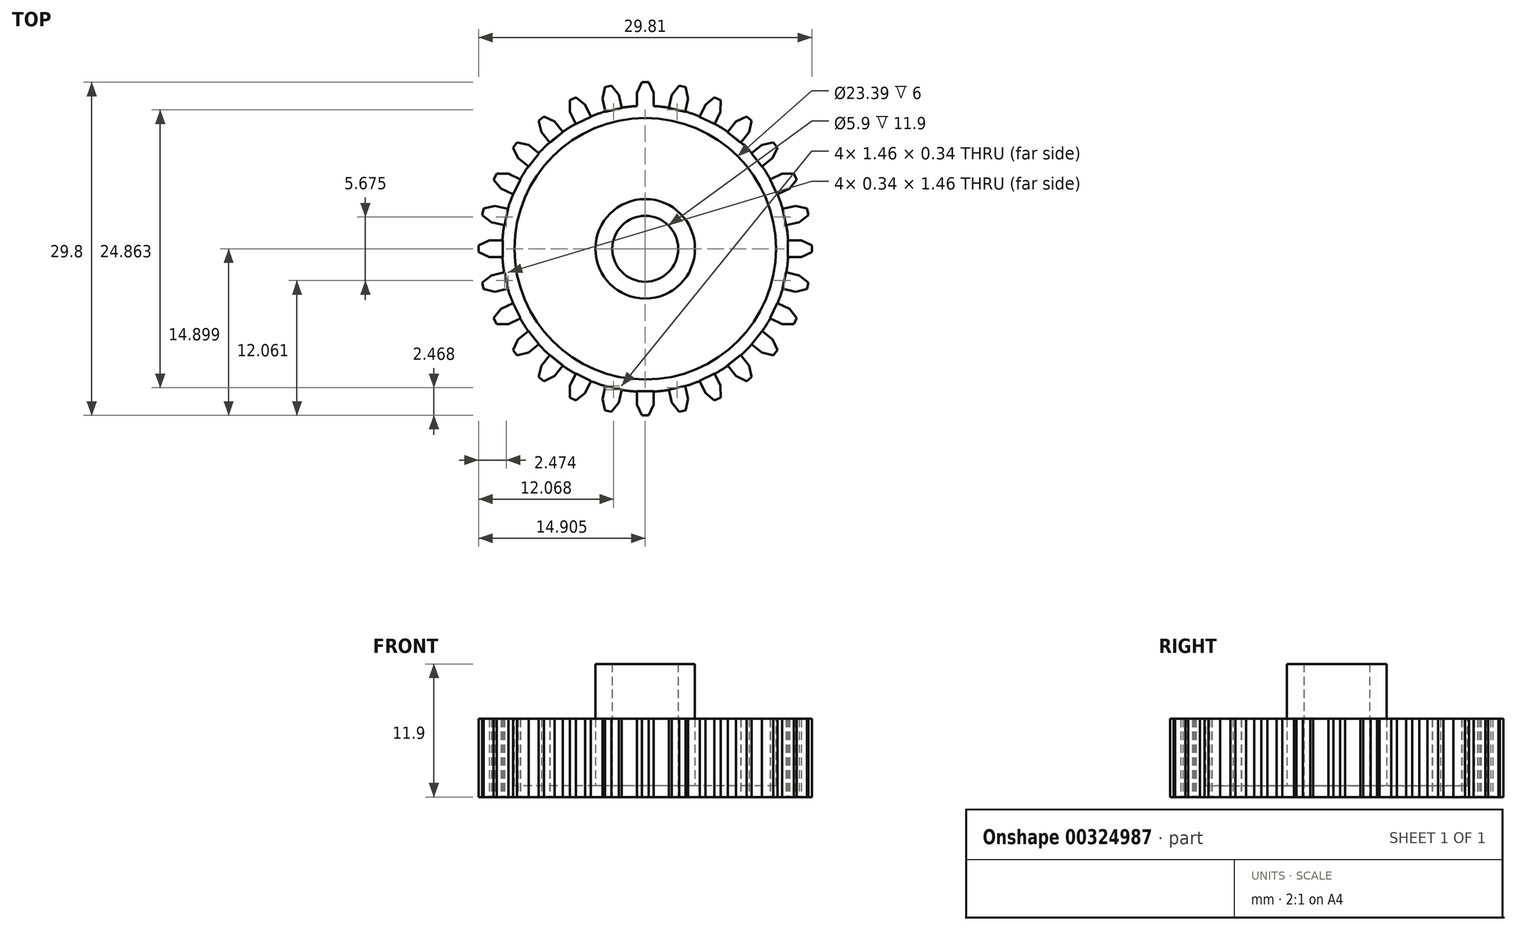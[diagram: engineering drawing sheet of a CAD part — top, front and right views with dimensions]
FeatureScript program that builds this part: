
annotation { "Feature Type Name" : "Feature", "Feature Type Description" : "" }
export const myFeature = defineFeature(function(context is Context, id is Id, definition is map)
    precondition{}
    {
        {
            var Q0;
            Q0=qCreatedBy(makeId("Top.planeOp"),FACE);
            var sketch = newSketch(context, id + "F0", { "sketchPlane" : qUnion([Q0])});
            skLineSegment(sketch, "E0", {"start": v(-37.42, 30.36) * mm, "end": v(-35.92, 30.36) * mm});
            skLineSegment(sketch, "E1", {"start": v(-36.97, 32.5) * mm, "end": v(-36.37, 32.5) * mm});
            skLineSegment(sketch, "E2", {"start": v(-37.42, 30.36) * mm, "end": v(-37.42, 31.56) * mm});
            skLineSegment(sketch, "E3", {"start": v(-37.42, 31.56) * mm, "end": v(-35.92, 31.56) * mm});
            skLineSegment(sketch, "E4", {"start": v(-35.92, 31.56) * mm, "end": v(-35.92, 30.36) * mm});
            skLineSegment(sketch, "E5", {"start": v(-36.97, 32.5) * mm, "end": v(-37.42, 31.56) * mm});
            skLineSegment(sketch, "E6", {"start": v(-36.37, 32.5) * mm, "end": v(-35.92, 31.56) * mm});
            skLineSegment(sketch, "E7.7.0", {"start": v(-36.98, 32.5) * mm, "end": v(-37.42, 31.56) * mm});
            skLineSegment(sketch, "E7.7.1", {"start": v(-35.92, 30.36) * mm, "end": v(-35.92, 31.56) * mm});
            skLineSegment(sketch, "E7.7.2", {"start": v(-36.67, 30.36) * mm, "end": v(-37.42, 30.36) * mm});
            skLineSegment(sketch, "E7.7.6", {"start": v(-36.67, 30.36) * mm, "end": v(-35.92, 30.36) * mm});
            skLineSegment(sketch, "E7.7.7", {"start": v(-36.67, 32.5) * mm, "end": v(-36.37, 32.5) * mm});
            skLineSegment(sketch, "E7.7.8", {"start": v(-36.67, 32.5) * mm, "end": v(-36.98, 32.5) * mm});
            skLineSegment(sketch, "E8", {"start": v(-36.67, 30.36) * mm, "end": v(-36.67, 4.86) * mm});
            skLineSegment(sketch, "E9", {"start": v(-36.67, 30.36) * mm, "end": v(-36.67, 17.6) * mm});
            skLineSegment(sketch, "E10.1.0", {"start": v(-40.24, 29.87) * mm, "end": v(-40.5, 31.04) * mm});
            skLineSegment(sketch, "E10.1.1", {"start": v(-38.78, 30.2) * mm, "end": v(-39.05, 31.38) * mm});
            skLineSegment(sketch, "E10.1.2", {"start": v(-40.5, 31.04) * mm, "end": v(-39.05, 31.38) * mm});
            skLineSegment(sketch, "E10.1.3", {"start": v(-40.29, 32.06) * mm, "end": v(-40.5, 31.04) * mm});
            skLineSegment(sketch, "E10.1.4", {"start": v(-39.7, 32.2) * mm, "end": v(-39.05, 31.38) * mm});
            skLineSegment(sketch, "E10.1.5", {"start": v(-40.24, 29.87) * mm, "end": v(-40.51, 31.04) * mm});
            skLineSegment(sketch, "E10.1.6", {"start": v(-39.05, 31.38) * mm, "end": v(-38.78, 30.2) * mm});
            skLineSegment(sketch, "E10.1.7", {"start": v(-40.51, 31.04) * mm, "end": v(-39.05, 31.38) * mm});
            skLineSegment(sketch, "E10.1.8", {"start": v(-40.28, 32.07) * mm, "end": v(-40.51, 31.04) * mm});
            skLineSegment(sketch, "E10.1.9", {"start": v(-39.7, 32.2) * mm, "end": v(-39.05, 31.38) * mm});
            skLineSegment(sketch, "E10.1.10", {"start": v(-39.51, 30.04) * mm, "end": v(-40.24, 29.87) * mm});
            skLineSegment(sketch, "E10.1.11", {"start": v(-40.24, 29.87) * mm, "end": v(-38.78, 30.2) * mm});
            skLineSegment(sketch, "E10.1.12", {"start": v(-39.51, 30.04) * mm, "end": v(-38.78, 30.2) * mm});
            skLineSegment(sketch, "E10.1.13", {"start": v(-40.28, 32.07) * mm, "end": v(-39.7, 32.2) * mm});
            skLineSegment(sketch, "E10.1.14", {"start": v(-39.99, 32.13) * mm, "end": v(-40.29, 32.06) * mm});
            skLineSegment(sketch, "E10.1.15", {"start": v(-39.99, 32.13) * mm, "end": v(-39.7, 32.2) * mm});
            skLineSegment(sketch, "E10.2.0", {"start": v(-42.88, 28.77) * mm, "end": v(-43.4, 29.85) * mm});
            skLineSegment(sketch, "E10.2.1", {"start": v(-41.53, 29.42) * mm, "end": v(-42.05, 30.5) * mm});
            skLineSegment(sketch, "E10.2.2", {"start": v(-43.4, 29.85) * mm, "end": v(-42.05, 30.5) * mm});
            skLineSegment(sketch, "E10.2.3", {"start": v(-43.4, 30.9) * mm, "end": v(-43.4, 29.85) * mm});
            skLineSegment(sketch, "E10.2.4", {"start": v(-42.86, 31.15) * mm, "end": v(-42.05, 30.5) * mm});
            skLineSegment(sketch, "E10.2.5", {"start": v(-42.88, 28.77) * mm, "end": v(-43.4, 29.85) * mm});
            skLineSegment(sketch, "E10.2.6", {"start": v(-42.05, 30.5) * mm, "end": v(-41.53, 29.42) * mm});
            skLineSegment(sketch, "E10.2.7", {"start": v(-43.4, 29.85) * mm, "end": v(-42.05, 30.5) * mm});
            skLineSegment(sketch, "E10.2.8", {"start": v(-43.41, 30.9) * mm, "end": v(-43.4, 29.85) * mm});
            skLineSegment(sketch, "E10.2.9", {"start": v(-42.87, 31.16) * mm, "end": v(-42.05, 30.5) * mm});
            skLineSegment(sketch, "E10.2.10", {"start": v(-42.2, 29.1) * mm, "end": v(-42.88, 28.77) * mm});
            skLineSegment(sketch, "E10.2.11", {"start": v(-42.88, 28.77) * mm, "end": v(-41.53, 29.42) * mm});
            skLineSegment(sketch, "E10.2.12", {"start": v(-42.2, 29.1) * mm, "end": v(-41.53, 29.42) * mm});
            skLineSegment(sketch, "E10.2.13", {"start": v(-43.41, 30.9) * mm, "end": v(-42.87, 31.16) * mm});
            skLineSegment(sketch, "E10.2.14", {"start": v(-43.14, 31.02) * mm, "end": v(-43.4, 30.9) * mm});
            skLineSegment(sketch, "E10.2.15", {"start": v(-43.14, 31.02) * mm, "end": v(-42.86, 31.15) * mm});
            skLineSegment(sketch, "E10.3.0", {"start": v(-45.21, 27.1) * mm, "end": v(-45.96, 28.05) * mm});
            skLineSegment(sketch, "E10.3.1", {"start": v(-44.04, 28.04) * mm, "end": v(-44.79, 28.98) * mm});
            skLineSegment(sketch, "E10.3.2", {"start": v(-45.96, 28.05) * mm, "end": v(-44.79, 28.98) * mm});
            skLineSegment(sketch, "E10.3.3", {"start": v(-46.2, 29.06) * mm, "end": v(-45.96, 28.05) * mm});
            skLineSegment(sketch, "E10.3.4", {"start": v(-45.72, 29.44) * mm, "end": v(-44.79, 28.98) * mm});
            skLineSegment(sketch, "E10.3.5", {"start": v(-45.21, 27.11) * mm, "end": v(-45.96, 28.05) * mm});
            skLineSegment(sketch, "E10.3.6", {"start": v(-44.79, 28.98) * mm, "end": v(-44.04, 28.05) * mm});
            skLineSegment(sketch, "E10.3.7", {"start": v(-45.96, 28.05) * mm, "end": v(-44.79, 28.98) * mm});
            skLineSegment(sketch, "E10.3.8", {"start": v(-46.2, 29.07) * mm, "end": v(-45.96, 28.05) * mm});
            skLineSegment(sketch, "E10.3.9", {"start": v(-45.73, 29.45) * mm, "end": v(-44.79, 28.98) * mm});
            skLineSegment(sketch, "E10.3.10", {"start": v(-44.62, 27.58) * mm, "end": v(-45.21, 27.1) * mm});
            skLineSegment(sketch, "E10.3.11", {"start": v(-45.21, 27.11) * mm, "end": v(-44.04, 28.05) * mm});
            skLineSegment(sketch, "E10.3.12", {"start": v(-44.62, 27.58) * mm, "end": v(-44.04, 28.04) * mm});
            skLineSegment(sketch, "E10.3.13", {"start": v(-46.2, 29.07) * mm, "end": v(-45.73, 29.45) * mm});
            skLineSegment(sketch, "E10.3.14", {"start": v(-45.96, 29.25) * mm, "end": v(-46.2, 29.06) * mm});
            skLineSegment(sketch, "E10.3.15", {"start": v(-45.96, 29.25) * mm, "end": v(-45.72, 29.44) * mm});
            skLineSegment(sketch, "E10.4.0", {"start": v(-47.11, 24.97) * mm, "end": v(-48.05, 25.72) * mm});
            skLineSegment(sketch, "E10.4.1", {"start": v(-46.18, 26.14) * mm, "end": v(-47.11, 26.9) * mm});
            skLineSegment(sketch, "E10.4.2", {"start": v(-48.05, 25.72) * mm, "end": v(-47.11, 26.9) * mm});
            skLineSegment(sketch, "E10.4.3", {"start": v(-48.5, 26.65) * mm, "end": v(-48.05, 25.72) * mm});
            skLineSegment(sketch, "E10.4.4", {"start": v(-48.13, 27.13) * mm, "end": v(-47.11, 26.9) * mm});
            skLineSegment(sketch, "E10.4.5", {"start": v(-47.11, 24.97) * mm, "end": v(-48.05, 25.72) * mm});
            skLineSegment(sketch, "E10.4.6", {"start": v(-47.12, 26.9) * mm, "end": v(-46.18, 26.15) * mm});
            skLineSegment(sketch, "E10.4.7", {"start": v(-48.05, 25.72) * mm, "end": v(-47.12, 26.9) * mm});
            skLineSegment(sketch, "E10.4.8", {"start": v(-48.51, 26.66) * mm, "end": v(-48.05, 25.72) * mm});
            skLineSegment(sketch, "E10.4.9", {"start": v(-48.14, 27.13) * mm, "end": v(-47.12, 26.9) * mm});
            skLineSegment(sketch, "E10.4.10", {"start": v(-46.64, 25.56) * mm, "end": v(-47.11, 24.97) * mm});
            skLineSegment(sketch, "E10.4.11", {"start": v(-47.11, 24.97) * mm, "end": v(-46.18, 26.15) * mm});
            skLineSegment(sketch, "E10.4.12", {"start": v(-46.64, 25.56) * mm, "end": v(-46.18, 26.14) * mm});
            skLineSegment(sketch, "E10.4.13", {"start": v(-48.51, 26.66) * mm, "end": v(-48.14, 27.13) * mm});
            skLineSegment(sketch, "E10.4.14", {"start": v(-48.32, 26.9) * mm, "end": v(-48.5, 26.65) * mm});
            skLineSegment(sketch, "E10.4.15", {"start": v(-48.32, 26.9) * mm, "end": v(-48.13, 27.13) * mm});
            skLineSegment(sketch, "E10.5.0", {"start": v(-48.49, 22.47) * mm, "end": v(-49.57, 22.99) * mm});
            skLineSegment(sketch, "E10.5.1", {"start": v(-47.84, 23.82) * mm, "end": v(-48.92, 24.34) * mm});
            skLineSegment(sketch, "E10.5.2", {"start": v(-49.57, 22.99) * mm, "end": v(-48.92, 24.34) * mm});
            skLineSegment(sketch, "E10.5.3", {"start": v(-50.22, 23.8) * mm, "end": v(-49.57, 22.99) * mm});
            skLineSegment(sketch, "E10.5.4", {"start": v(-49.96, 24.34) * mm, "end": v(-48.92, 24.34) * mm});
            skLineSegment(sketch, "E10.5.5", {"start": v(-48.49, 22.47) * mm, "end": v(-49.57, 22.99) * mm});
            skLineSegment(sketch, "E10.5.6", {"start": v(-48.92, 24.34) * mm, "end": v(-47.84, 23.82) * mm});
            skLineSegment(sketch, "E10.5.7", {"start": v(-49.57, 22.99) * mm, "end": v(-48.92, 24.34) * mm});
            skLineSegment(sketch, "E10.5.8", {"start": v(-50.23, 23.8) * mm, "end": v(-49.57, 22.99) * mm});
            skLineSegment(sketch, "E10.5.9", {"start": v(-49.97, 24.34) * mm, "end": v(-48.92, 24.34) * mm});
            skLineSegment(sketch, "E10.5.10", {"start": v(-48.16, 23.14) * mm, "end": v(-48.49, 22.47) * mm});
            skLineSegment(sketch, "E10.5.11", {"start": v(-48.49, 22.47) * mm, "end": v(-47.84, 23.82) * mm});
            skLineSegment(sketch, "E10.5.12", {"start": v(-48.16, 23.14) * mm, "end": v(-47.84, 23.82) * mm});
            skLineSegment(sketch, "E10.5.13", {"start": v(-50.23, 23.8) * mm, "end": v(-49.97, 24.34) * mm});
            skLineSegment(sketch, "E10.5.14", {"start": v(-50.09, 24.07) * mm, "end": v(-50.22, 23.8) * mm});
            skLineSegment(sketch, "E10.5.15", {"start": v(-50.09, 24.07) * mm, "end": v(-49.96, 24.34) * mm});
            skLineSegment(sketch, "E10.6.0", {"start": v(-49.27, 19.71) * mm, "end": v(-50.44, 19.98) * mm});
            skLineSegment(sketch, "E10.6.1", {"start": v(-48.94, 21.18) * mm, "end": v(-50.1, 21.44) * mm});
            skLineSegment(sketch, "E10.6.2", {"start": v(-50.44, 19.98) * mm, "end": v(-50.1, 21.44) * mm});
            skLineSegment(sketch, "E10.6.3", {"start": v(-51.26, 20.63) * mm, "end": v(-50.44, 19.98) * mm});
            skLineSegment(sketch, "E10.6.4", {"start": v(-51.12, 21.21) * mm, "end": v(-50.1, 21.44) * mm});
            skLineSegment(sketch, "E10.6.5", {"start": v(-49.27, 19.72) * mm, "end": v(-50.44, 19.98) * mm});
            skLineSegment(sketch, "E10.6.6", {"start": v(-50.11, 21.44) * mm, "end": v(-48.94, 21.18) * mm});
            skLineSegment(sketch, "E10.6.7", {"start": v(-50.44, 19.98) * mm, "end": v(-50.11, 21.44) * mm});
            skLineSegment(sketch, "E10.6.8", {"start": v(-51.27, 20.63) * mm, "end": v(-50.44, 19.98) * mm});
            skLineSegment(sketch, "E10.6.9", {"start": v(-51.14, 21.22) * mm, "end": v(-50.11, 21.44) * mm});
            skLineSegment(sketch, "E10.6.10", {"start": v(-49.1, 20.45) * mm, "end": v(-49.27, 19.71) * mm});
            skLineSegment(sketch, "E10.6.11", {"start": v(-49.27, 19.72) * mm, "end": v(-48.94, 21.18) * mm});
            skLineSegment(sketch, "E10.6.12", {"start": v(-49.1, 20.45) * mm, "end": v(-48.94, 21.18) * mm});
            skLineSegment(sketch, "E10.6.13", {"start": v(-51.27, 20.63) * mm, "end": v(-51.14, 21.22) * mm});
            skLineSegment(sketch, "E10.6.14", {"start": v(-51.2, 20.92) * mm, "end": v(-51.26, 20.63) * mm});
            skLineSegment(sketch, "E10.6.15", {"start": v(-51.2, 20.92) * mm, "end": v(-51.12, 21.21) * mm});
            skLineSegment(sketch, "E10.7.0", {"start": v(-49.42, 16.86) * mm, "end": v(-50.62, 16.86) * mm});
            skLineSegment(sketch, "E10.7.1", {"start": v(-49.42, 18.36) * mm, "end": v(-50.62, 18.36) * mm});
            skLineSegment(sketch, "E10.7.2", {"start": v(-50.62, 16.86) * mm, "end": v(-50.62, 18.36) * mm});
            skLineSegment(sketch, "E10.7.3", {"start": v(-51.56, 17.3) * mm, "end": v(-50.62, 16.86) * mm});
            skLineSegment(sketch, "E10.7.4", {"start": v(-51.56, 17.9) * mm, "end": v(-50.62, 18.36) * mm});
            skLineSegment(sketch, "E10.7.5", {"start": v(-49.43, 16.86) * mm, "end": v(-50.63, 16.86) * mm});
            skLineSegment(sketch, "E10.7.6", {"start": v(-50.63, 18.36) * mm, "end": v(-49.43, 18.36) * mm});
            skLineSegment(sketch, "E10.7.7", {"start": v(-50.63, 16.86) * mm, "end": v(-50.63, 18.36) * mm});
            skLineSegment(sketch, "E10.7.8", {"start": v(-51.58, 17.3) * mm, "end": v(-50.63, 16.86) * mm});
            skLineSegment(sketch, "E10.7.9", {"start": v(-51.58, 17.9) * mm, "end": v(-50.63, 18.36) * mm});
            skLineSegment(sketch, "E10.7.10", {"start": v(-49.42, 17.6) * mm, "end": v(-49.42, 16.86) * mm});
            skLineSegment(sketch, "E10.7.11", {"start": v(-49.43, 16.86) * mm, "end": v(-49.43, 18.36) * mm});
            skLineSegment(sketch, "E10.7.12", {"start": v(-49.42, 17.6) * mm, "end": v(-49.42, 18.36) * mm});
            skLineSegment(sketch, "E10.7.13", {"start": v(-51.58, 17.3) * mm, "end": v(-51.58, 17.9) * mm});
            skLineSegment(sketch, "E10.7.14", {"start": v(-51.56, 17.6) * mm, "end": v(-51.56, 17.3) * mm});
            skLineSegment(sketch, "E10.7.15", {"start": v(-51.56, 17.6) * mm, "end": v(-51.56, 17.9) * mm});
            skLineSegment(sketch, "E10.8.0", {"start": v(-48.94, 14.04) * mm, "end": v(-50.1, 13.77) * mm});
            skLineSegment(sketch, "E10.8.1", {"start": v(-49.27, 15.5) * mm, "end": v(-50.44, 15.24) * mm});
            skLineSegment(sketch, "E10.8.2", {"start": v(-50.1, 13.77) * mm, "end": v(-50.44, 15.24) * mm});
            skLineSegment(sketch, "E10.8.3", {"start": v(-51.12, 14) * mm, "end": v(-50.1, 13.77) * mm});
            skLineSegment(sketch, "E10.8.4", {"start": v(-51.26, 14.59) * mm, "end": v(-50.44, 15.24) * mm});
            skLineSegment(sketch, "E10.8.5", {"start": v(-48.94, 14.04) * mm, "end": v(-50.11, 13.77) * mm});
            skLineSegment(sketch, "E10.8.6", {"start": v(-50.44, 15.24) * mm, "end": v(-49.27, 15.5) * mm});
            skLineSegment(sketch, "E10.8.7", {"start": v(-50.11, 13.77) * mm, "end": v(-50.44, 15.24) * mm});
            skLineSegment(sketch, "E10.8.8", {"start": v(-51.14, 14) * mm, "end": v(-50.11, 13.77) * mm});
            skLineSegment(sketch, "E10.8.9", {"start": v(-51.27, 14.59) * mm, "end": v(-50.44, 15.24) * mm});
            skLineSegment(sketch, "E10.8.10", {"start": v(-49.1, 14.77) * mm, "end": v(-48.94, 14.04) * mm});
            skLineSegment(sketch, "E10.8.11", {"start": v(-48.94, 14.04) * mm, "end": v(-49.27, 15.5) * mm});
            skLineSegment(sketch, "E10.8.12", {"start": v(-49.1, 14.77) * mm, "end": v(-49.27, 15.5) * mm});
            skLineSegment(sketch, "E10.8.13", {"start": v(-51.14, 14) * mm, "end": v(-51.27, 14.59) * mm});
            skLineSegment(sketch, "E10.8.14", {"start": v(-51.2, 14.3) * mm, "end": v(-51.12, 14) * mm});
            skLineSegment(sketch, "E10.8.15", {"start": v(-51.2, 14.3) * mm, "end": v(-51.26, 14.59) * mm});
            skLineSegment(sketch, "E10.9.0", {"start": v(-47.84, 11.4) * mm, "end": v(-48.92, 10.88) * mm});
            skLineSegment(sketch, "E10.9.1", {"start": v(-48.49, 12.75) * mm, "end": v(-49.57, 12.23) * mm});
            skLineSegment(sketch, "E10.9.2", {"start": v(-48.92, 10.88) * mm, "end": v(-49.57, 12.23) * mm});
            skLineSegment(sketch, "E10.9.3", {"start": v(-49.96, 10.87) * mm, "end": v(-48.92, 10.88) * mm});
            skLineSegment(sketch, "E10.9.4", {"start": v(-50.22, 11.42) * mm, "end": v(-49.57, 12.23) * mm});
            skLineSegment(sketch, "E10.9.5", {"start": v(-47.84, 11.4) * mm, "end": v(-48.92, 10.88) * mm});
            skLineSegment(sketch, "E10.9.6", {"start": v(-49.57, 12.23) * mm, "end": v(-48.49, 12.75) * mm});
            skLineSegment(sketch, "E10.9.7", {"start": v(-48.92, 10.88) * mm, "end": v(-49.57, 12.23) * mm});
            skLineSegment(sketch, "E10.9.8", {"start": v(-49.97, 10.87) * mm, "end": v(-48.92, 10.88) * mm});
            skLineSegment(sketch, "E10.9.9", {"start": v(-50.23, 11.41) * mm, "end": v(-49.57, 12.23) * mm});
            skLineSegment(sketch, "E10.9.10", {"start": v(-48.16, 12.08) * mm, "end": v(-47.84, 11.4) * mm});
            skLineSegment(sketch, "E10.9.11", {"start": v(-47.84, 11.4) * mm, "end": v(-48.49, 12.75) * mm});
            skLineSegment(sketch, "E10.9.12", {"start": v(-48.16, 12.08) * mm, "end": v(-48.49, 12.75) * mm});
            skLineSegment(sketch, "E10.9.13", {"start": v(-49.97, 10.87) * mm, "end": v(-50.23, 11.41) * mm});
            skLineSegment(sketch, "E10.9.14", {"start": v(-50.09, 11.15) * mm, "end": v(-49.96, 10.87) * mm});
            skLineSegment(sketch, "E10.9.15", {"start": v(-50.09, 11.15) * mm, "end": v(-50.22, 11.42) * mm});
            skLineSegment(sketch, "E10.10.0", {"start": v(-46.18, 9.07) * mm, "end": v(-47.11, 8.32) * mm});
            skLineSegment(sketch, "E10.10.1", {"start": v(-47.11, 10.25) * mm, "end": v(-48.05, 9.5) * mm});
            skLineSegment(sketch, "E10.10.2", {"start": v(-47.11, 8.32) * mm, "end": v(-48.05, 9.5) * mm});
            skLineSegment(sketch, "E10.10.3", {"start": v(-48.13, 8.09) * mm, "end": v(-47.11, 8.32) * mm});
            skLineSegment(sketch, "E10.10.4", {"start": v(-48.5, 8.56) * mm, "end": v(-48.05, 9.5) * mm});
            skLineSegment(sketch, "E10.10.5", {"start": v(-46.18, 9.07) * mm, "end": v(-47.12, 8.32) * mm});
            skLineSegment(sketch, "E10.10.6", {"start": v(-48.05, 9.5) * mm, "end": v(-47.11, 10.24) * mm});
            skLineSegment(sketch, "E10.10.7", {"start": v(-47.12, 8.32) * mm, "end": v(-48.05, 9.5) * mm});
            skLineSegment(sketch, "E10.10.8", {"start": v(-48.14, 8.08) * mm, "end": v(-47.12, 8.32) * mm});
            skLineSegment(sketch, "E10.10.9", {"start": v(-48.51, 8.55) * mm, "end": v(-48.05, 9.5) * mm});
            skLineSegment(sketch, "E10.10.10", {"start": v(-46.64, 9.66) * mm, "end": v(-46.18, 9.07) * mm});
            skLineSegment(sketch, "E10.10.11", {"start": v(-46.18, 9.07) * mm, "end": v(-47.11, 10.24) * mm});
            skLineSegment(sketch, "E10.10.12", {"start": v(-46.64, 9.66) * mm, "end": v(-47.11, 10.25) * mm});
            skLineSegment(sketch, "E10.10.13", {"start": v(-48.14, 8.08) * mm, "end": v(-48.51, 8.55) * mm});
            skLineSegment(sketch, "E10.10.14", {"start": v(-48.32, 8.33) * mm, "end": v(-48.13, 8.09) * mm});
            skLineSegment(sketch, "E10.10.15", {"start": v(-48.32, 8.33) * mm, "end": v(-48.5, 8.56) * mm});
            skLineSegment(sketch, "E10.11.0", {"start": v(-44.04, 7.17) * mm, "end": v(-44.79, 6.23) * mm});
            skLineSegment(sketch, "E10.11.1", {"start": v(-45.21, 8.1) * mm, "end": v(-45.96, 7.17) * mm});
            skLineSegment(sketch, "E10.11.2", {"start": v(-44.79, 6.23) * mm, "end": v(-45.96, 7.17) * mm});
            skLineSegment(sketch, "E10.11.3", {"start": v(-45.72, 5.78) * mm, "end": v(-44.79, 6.23) * mm});
            skLineSegment(sketch, "E10.11.4", {"start": v(-46.2, 6.15) * mm, "end": v(-45.96, 7.17) * mm});
            skLineSegment(sketch, "E10.11.5", {"start": v(-44.04, 7.17) * mm, "end": v(-44.79, 6.23) * mm});
            skLineSegment(sketch, "E10.11.6", {"start": v(-45.96, 7.17) * mm, "end": v(-45.21, 8.1) * mm});
            skLineSegment(sketch, "E10.11.7", {"start": v(-44.79, 6.23) * mm, "end": v(-45.96, 7.17) * mm});
            skLineSegment(sketch, "E10.11.8", {"start": v(-45.73, 5.77) * mm, "end": v(-44.79, 6.23) * mm});
            skLineSegment(sketch, "E10.11.9", {"start": v(-46.2, 6.15) * mm, "end": v(-45.96, 7.17) * mm});
            skLineSegment(sketch, "E10.11.10", {"start": v(-44.62, 7.64) * mm, "end": v(-44.04, 7.17) * mm});
            skLineSegment(sketch, "E10.11.11", {"start": v(-44.04, 7.17) * mm, "end": v(-45.21, 8.1) * mm});
            skLineSegment(sketch, "E10.11.12", {"start": v(-44.62, 7.64) * mm, "end": v(-45.21, 8.1) * mm});
            skLineSegment(sketch, "E10.11.13", {"start": v(-45.73, 5.77) * mm, "end": v(-46.2, 6.15) * mm});
            skLineSegment(sketch, "E10.11.14", {"start": v(-45.96, 5.97) * mm, "end": v(-45.72, 5.78) * mm});
            skLineSegment(sketch, "E10.11.15", {"start": v(-45.96, 5.97) * mm, "end": v(-46.2, 6.15) * mm});
            skLineSegment(sketch, "E10.12.0", {"start": v(-41.53, 5.8) * mm, "end": v(-42.05, 4.71) * mm});
            skLineSegment(sketch, "E10.12.1", {"start": v(-42.88, 6.45) * mm, "end": v(-43.4, 5.37) * mm});
            skLineSegment(sketch, "E10.12.2", {"start": v(-42.05, 4.71) * mm, "end": v(-43.4, 5.37) * mm});
            skLineSegment(sketch, "E10.12.3", {"start": v(-42.86, 4.06) * mm, "end": v(-42.05, 4.71) * mm});
            skLineSegment(sketch, "E10.12.4", {"start": v(-43.4, 4.32) * mm, "end": v(-43.4, 5.37) * mm});
            skLineSegment(sketch, "E10.12.5", {"start": v(-41.53, 5.8) * mm, "end": v(-42.05, 4.71) * mm});
            skLineSegment(sketch, "E10.12.6", {"start": v(-43.4, 5.36) * mm, "end": v(-42.88, 6.45) * mm});
            skLineSegment(sketch, "E10.12.7", {"start": v(-42.05, 4.71) * mm, "end": v(-43.4, 5.36) * mm});
            skLineSegment(sketch, "E10.12.8", {"start": v(-42.87, 4.05) * mm, "end": v(-42.05, 4.71) * mm});
            skLineSegment(sketch, "E10.12.9", {"start": v(-43.41, 4.31) * mm, "end": v(-43.4, 5.36) * mm});
            skLineSegment(sketch, "E10.12.10", {"start": v(-42.2, 6.12) * mm, "end": v(-41.53, 5.8) * mm});
            skLineSegment(sketch, "E10.12.11", {"start": v(-41.53, 5.8) * mm, "end": v(-42.88, 6.45) * mm});
            skLineSegment(sketch, "E10.12.12", {"start": v(-42.2, 6.12) * mm, "end": v(-42.88, 6.45) * mm});
            skLineSegment(sketch, "E10.12.13", {"start": v(-42.87, 4.05) * mm, "end": v(-43.41, 4.31) * mm});
            skLineSegment(sketch, "E10.12.14", {"start": v(-43.14, 4.2) * mm, "end": v(-42.86, 4.06) * mm});
            skLineSegment(sketch, "E10.12.15", {"start": v(-43.14, 4.2) * mm, "end": v(-43.4, 4.32) * mm});
            skLineSegment(sketch, "E10.13.0", {"start": v(-38.78, 5.01) * mm, "end": v(-39.05, 3.84) * mm});
            skLineSegment(sketch, "E10.13.1", {"start": v(-40.24, 5.35) * mm, "end": v(-40.5, 4.18) * mm});
            skLineSegment(sketch, "E10.13.2", {"start": v(-39.05, 3.84) * mm, "end": v(-40.5, 4.18) * mm});
            skLineSegment(sketch, "E10.13.3", {"start": v(-39.7, 3.02) * mm, "end": v(-39.05, 3.84) * mm});
            skLineSegment(sketch, "E10.13.4", {"start": v(-40.28, 3.16) * mm, "end": v(-40.5, 4.18) * mm});
            skLineSegment(sketch, "E10.13.5", {"start": v(-38.78, 5) * mm, "end": v(-39.05, 3.84) * mm});
            skLineSegment(sketch, "E10.13.6", {"start": v(-40.51, 4.17) * mm, "end": v(-40.24, 5.34) * mm});
            skLineSegment(sketch, "E10.13.7", {"start": v(-39.05, 3.84) * mm, "end": v(-40.51, 4.17) * mm});
            skLineSegment(sketch, "E10.13.8", {"start": v(-39.7, 3.01) * mm, "end": v(-39.05, 3.84) * mm});
            skLineSegment(sketch, "E10.13.9", {"start": v(-40.28, 3.15) * mm, "end": v(-40.51, 4.17) * mm});
            skLineSegment(sketch, "E10.13.10", {"start": v(-39.51, 5.18) * mm, "end": v(-38.78, 5.01) * mm});
            skLineSegment(sketch, "E10.13.11", {"start": v(-38.78, 5) * mm, "end": v(-40.24, 5.34) * mm});
            skLineSegment(sketch, "E10.13.12", {"start": v(-39.51, 5.18) * mm, "end": v(-40.24, 5.35) * mm});
            skLineSegment(sketch, "E10.13.13", {"start": v(-39.7, 3.01) * mm, "end": v(-40.28, 3.15) * mm});
            skLineSegment(sketch, "E10.13.14", {"start": v(-39.99, 3.1) * mm, "end": v(-39.7, 3.02) * mm});
            skLineSegment(sketch, "E10.13.15", {"start": v(-39.99, 3.1) * mm, "end": v(-40.28, 3.16) * mm});
            skLineSegment(sketch, "E10.14.0", {"start": v(-35.92, 4.86) * mm, "end": v(-35.92, 3.66) * mm});
            skLineSegment(sketch, "E10.14.1", {"start": v(-37.42, 4.86) * mm, "end": v(-37.42, 3.66) * mm});
            skLineSegment(sketch, "E10.14.2", {"start": v(-35.92, 3.66) * mm, "end": v(-37.42, 3.66) * mm});
            skLineSegment(sketch, "E10.14.3", {"start": v(-36.37, 2.72) * mm, "end": v(-35.92, 3.66) * mm});
            skLineSegment(sketch, "E10.14.4", {"start": v(-36.97, 2.72) * mm, "end": v(-37.42, 3.66) * mm});
            skLineSegment(sketch, "E10.14.5", {"start": v(-35.92, 4.86) * mm, "end": v(-35.92, 3.66) * mm});
            skLineSegment(sketch, "E10.14.6", {"start": v(-37.42, 3.66) * mm, "end": v(-37.42, 4.86) * mm});
            skLineSegment(sketch, "E10.14.7", {"start": v(-35.92, 3.66) * mm, "end": v(-37.42, 3.66) * mm});
            skLineSegment(sketch, "E10.14.8", {"start": v(-36.37, 2.7) * mm, "end": v(-35.92, 3.66) * mm});
            skLineSegment(sketch, "E10.14.9", {"start": v(-36.97, 2.7) * mm, "end": v(-37.42, 3.66) * mm});
            skLineSegment(sketch, "E10.14.10", {"start": v(-36.67, 4.86) * mm, "end": v(-35.92, 4.86) * mm});
            skLineSegment(sketch, "E10.14.11", {"start": v(-35.92, 4.86) * mm, "end": v(-37.42, 4.86) * mm});
            skLineSegment(sketch, "E10.14.12", {"start": v(-36.67, 4.86) * mm, "end": v(-37.42, 4.86) * mm});
            skLineSegment(sketch, "E10.14.13", {"start": v(-36.37, 2.7) * mm, "end": v(-36.97, 2.7) * mm});
            skLineSegment(sketch, "E10.14.14", {"start": v(-36.67, 2.72) * mm, "end": v(-36.37, 2.72) * mm});
            skLineSegment(sketch, "E10.14.15", {"start": v(-36.67, 2.72) * mm, "end": v(-36.97, 2.72) * mm});
            skLineSegment(sketch, "E10.15.0", {"start": v(-33.1, 5.35) * mm, "end": v(-32.84, 4.18) * mm});
            skLineSegment(sketch, "E10.15.1", {"start": v(-34.57, 5.01) * mm, "end": v(-34.3, 3.84) * mm});
            skLineSegment(sketch, "E10.15.2", {"start": v(-32.84, 4.18) * mm, "end": v(-34.3, 3.84) * mm});
            skLineSegment(sketch, "E10.15.3", {"start": v(-33.06, 3.16) * mm, "end": v(-32.84, 4.18) * mm});
            skLineSegment(sketch, "E10.15.4", {"start": v(-33.65, 3.03) * mm, "end": v(-34.3, 3.84) * mm});
            skLineSegment(sketch, "E10.15.5", {"start": v(-33.1, 5.34) * mm, "end": v(-32.84, 4.17) * mm});
            skLineSegment(sketch, "E10.15.6", {"start": v(-34.3, 3.84) * mm, "end": v(-34.57, 5) * mm});
            skLineSegment(sketch, "E10.15.7", {"start": v(-32.84, 4.17) * mm, "end": v(-34.3, 3.84) * mm});
            skLineSegment(sketch, "E10.15.8", {"start": v(-33.07, 3.15) * mm, "end": v(-32.84, 4.17) * mm});
            skLineSegment(sketch, "E10.15.9", {"start": v(-33.65, 3.01) * mm, "end": v(-34.3, 3.84) * mm});
            skLineSegment(sketch, "E10.15.10", {"start": v(-33.84, 5.18) * mm, "end": v(-33.1, 5.35) * mm});
            skLineSegment(sketch, "E10.15.11", {"start": v(-33.1, 5.34) * mm, "end": v(-34.57, 5) * mm});
            skLineSegment(sketch, "E10.15.12", {"start": v(-33.84, 5.18) * mm, "end": v(-34.57, 5.01) * mm});
            skLineSegment(sketch, "E10.15.13", {"start": v(-33.07, 3.15) * mm, "end": v(-33.65, 3.01) * mm});
            skLineSegment(sketch, "E10.15.14", {"start": v(-33.36, 3.1) * mm, "end": v(-33.06, 3.16) * mm});
            skLineSegment(sketch, "E10.15.15", {"start": v(-33.36, 3.1) * mm, "end": v(-33.65, 3.03) * mm});
            skLineSegment(sketch, "E10.16.0", {"start": v(-30.47, 6.45) * mm, "end": v(-29.95, 5.37) * mm});
            skLineSegment(sketch, "E10.16.1", {"start": v(-31.82, 5.8) * mm, "end": v(-31.3, 4.71) * mm});
            skLineSegment(sketch, "E10.16.2", {"start": v(-29.95, 5.37) * mm, "end": v(-31.3, 4.71) * mm});
            skLineSegment(sketch, "E10.16.3", {"start": v(-29.94, 4.33) * mm, "end": v(-29.95, 5.37) * mm});
            skLineSegment(sketch, "E10.16.4", {"start": v(-30.48, 4.06) * mm, "end": v(-31.3, 4.71) * mm});
            skLineSegment(sketch, "E10.16.5", {"start": v(-30.47, 6.45) * mm, "end": v(-29.95, 5.36) * mm});
            skLineSegment(sketch, "E10.16.6", {"start": v(-31.3, 4.71) * mm, "end": v(-31.82, 5.8) * mm});
            skLineSegment(sketch, "E10.16.7", {"start": v(-29.95, 5.36) * mm, "end": v(-31.3, 4.71) * mm});
            skLineSegment(sketch, "E10.16.8", {"start": v(-29.94, 4.31) * mm, "end": v(-29.95, 5.36) * mm});
            skLineSegment(sketch, "E10.16.9", {"start": v(-30.48, 4.05) * mm, "end": v(-31.3, 4.71) * mm});
            skLineSegment(sketch, "E10.16.10", {"start": v(-31.14, 6.12) * mm, "end": v(-30.47, 6.45) * mm});
            skLineSegment(sketch, "E10.16.11", {"start": v(-30.47, 6.45) * mm, "end": v(-31.82, 5.8) * mm});
            skLineSegment(sketch, "E10.16.12", {"start": v(-31.14, 6.12) * mm, "end": v(-31.82, 5.8) * mm});
            skLineSegment(sketch, "E10.16.13", {"start": v(-29.94, 4.31) * mm, "end": v(-30.48, 4.05) * mm});
            skLineSegment(sketch, "E10.16.14", {"start": v(-30.21, 4.2) * mm, "end": v(-29.94, 4.33) * mm});
            skLineSegment(sketch, "E10.16.15", {"start": v(-30.21, 4.2) * mm, "end": v(-30.48, 4.06) * mm});
            skLineSegment(sketch, "E10.17.0", {"start": v(-28.14, 8.1) * mm, "end": v(-27.4, 7.17) * mm});
            skLineSegment(sketch, "E10.17.1", {"start": v(-29.31, 7.17) * mm, "end": v(-28.56, 6.23) * mm});
            skLineSegment(sketch, "E10.17.2", {"start": v(-27.4, 7.17) * mm, "end": v(-28.56, 6.23) * mm});
            skLineSegment(sketch, "E10.17.3", {"start": v(-27.15, 6.16) * mm, "end": v(-27.4, 7.17) * mm});
            skLineSegment(sketch, "E10.17.4", {"start": v(-27.63, 5.78) * mm, "end": v(-28.56, 6.23) * mm});
            skLineSegment(sketch, "E10.17.5", {"start": v(-28.14, 8.1) * mm, "end": v(-27.39, 7.17) * mm});
            skLineSegment(sketch, "E10.17.6", {"start": v(-28.56, 6.23) * mm, "end": v(-29.31, 7.17) * mm});
            skLineSegment(sketch, "E10.17.7", {"start": v(-27.39, 7.17) * mm, "end": v(-28.56, 6.23) * mm});
            skLineSegment(sketch, "E10.17.8", {"start": v(-27.15, 6.15) * mm, "end": v(-27.39, 7.17) * mm});
            skLineSegment(sketch, "E10.17.9", {"start": v(-27.62, 5.77) * mm, "end": v(-28.56, 6.23) * mm});
            skLineSegment(sketch, "E10.17.10", {"start": v(-28.73, 7.64) * mm, "end": v(-28.14, 8.1) * mm});
            skLineSegment(sketch, "E10.17.11", {"start": v(-28.14, 8.1) * mm, "end": v(-29.31, 7.17) * mm});
            skLineSegment(sketch, "E10.17.12", {"start": v(-28.73, 7.64) * mm, "end": v(-29.31, 7.17) * mm});
            skLineSegment(sketch, "E10.17.13", {"start": v(-27.15, 6.15) * mm, "end": v(-27.62, 5.77) * mm});
            skLineSegment(sketch, "E10.17.14", {"start": v(-27.4, 5.97) * mm, "end": v(-27.15, 6.16) * mm});
            skLineSegment(sketch, "E10.17.15", {"start": v(-27.4, 5.97) * mm, "end": v(-27.63, 5.78) * mm});
            skLineSegment(sketch, "E10.18.0", {"start": v(-26.24, 10.25) * mm, "end": v(-25.3, 9.5) * mm});
            skLineSegment(sketch, "E10.18.1", {"start": v(-27.17, 9.07) * mm, "end": v(-26.24, 8.32) * mm});
            skLineSegment(sketch, "E10.18.2", {"start": v(-25.3, 9.5) * mm, "end": v(-26.24, 8.32) * mm});
            skLineSegment(sketch, "E10.18.3", {"start": v(-24.84, 8.56) * mm, "end": v(-25.3, 9.5) * mm});
            skLineSegment(sketch, "E10.18.4", {"start": v(-25.22, 8.1) * mm, "end": v(-26.24, 8.32) * mm});
            skLineSegment(sketch, "E10.18.5", {"start": v(-26.24, 10.24) * mm, "end": v(-25.3, 9.5) * mm});
            skLineSegment(sketch, "E10.18.6", {"start": v(-26.23, 8.32) * mm, "end": v(-27.17, 9.07) * mm});
            skLineSegment(sketch, "E10.18.7", {"start": v(-25.3, 9.5) * mm, "end": v(-26.23, 8.32) * mm});
            skLineSegment(sketch, "E10.18.8", {"start": v(-24.84, 8.55) * mm, "end": v(-25.3, 9.5) * mm});
            skLineSegment(sketch, "E10.18.9", {"start": v(-25.21, 8.08) * mm, "end": v(-26.23, 8.32) * mm});
            skLineSegment(sketch, "E10.18.10", {"start": v(-26.7, 9.66) * mm, "end": v(-26.24, 10.25) * mm});
            skLineSegment(sketch, "E10.18.11", {"start": v(-26.24, 10.24) * mm, "end": v(-27.17, 9.07) * mm});
            skLineSegment(sketch, "E10.18.12", {"start": v(-26.7, 9.66) * mm, "end": v(-27.17, 9.07) * mm});
            skLineSegment(sketch, "E10.18.13", {"start": v(-24.84, 8.55) * mm, "end": v(-25.21, 8.08) * mm});
            skLineSegment(sketch, "E10.18.14", {"start": v(-25.03, 8.33) * mm, "end": v(-24.84, 8.56) * mm});
            skLineSegment(sketch, "E10.18.15", {"start": v(-25.03, 8.33) * mm, "end": v(-25.22, 8.1) * mm});
            skLineSegment(sketch, "E10.19.0", {"start": v(-24.86, 12.75) * mm, "end": v(-23.78, 12.23) * mm});
            skLineSegment(sketch, "E10.19.1", {"start": v(-25.51, 11.4) * mm, "end": v(-24.43, 10.88) * mm});
            skLineSegment(sketch, "E10.19.2", {"start": v(-23.78, 12.23) * mm, "end": v(-24.43, 10.88) * mm});
            skLineSegment(sketch, "E10.19.3", {"start": v(-23.13, 11.42) * mm, "end": v(-23.78, 12.23) * mm});
            skLineSegment(sketch, "E10.19.4", {"start": v(-23.39, 10.88) * mm, "end": v(-24.43, 10.88) * mm});
            skLineSegment(sketch, "E10.19.5", {"start": v(-24.86, 12.75) * mm, "end": v(-23.78, 12.23) * mm});
            skLineSegment(sketch, "E10.19.6", {"start": v(-24.43, 10.88) * mm, "end": v(-25.51, 11.4) * mm});
            skLineSegment(sketch, "E10.19.7", {"start": v(-23.78, 12.23) * mm, "end": v(-24.43, 10.88) * mm});
            skLineSegment(sketch, "E10.19.8", {"start": v(-23.12, 11.41) * mm, "end": v(-23.78, 12.23) * mm});
            skLineSegment(sketch, "E10.19.9", {"start": v(-23.38, 10.87) * mm, "end": v(-24.43, 10.88) * mm});
            skLineSegment(sketch, "E10.19.10", {"start": v(-25.19, 12.08) * mm, "end": v(-24.86, 12.75) * mm});
            skLineSegment(sketch, "E10.19.11", {"start": v(-24.86, 12.75) * mm, "end": v(-25.51, 11.4) * mm});
            skLineSegment(sketch, "E10.19.12", {"start": v(-25.19, 12.08) * mm, "end": v(-25.51, 11.4) * mm});
            skLineSegment(sketch, "E10.19.13", {"start": v(-23.12, 11.41) * mm, "end": v(-23.38, 10.87) * mm});
            skLineSegment(sketch, "E10.19.14", {"start": v(-23.26, 11.15) * mm, "end": v(-23.13, 11.42) * mm});
            skLineSegment(sketch, "E10.19.15", {"start": v(-23.26, 11.15) * mm, "end": v(-23.39, 10.88) * mm});
            skLineSegment(sketch, "E10.20.0", {"start": v(-24.08, 15.5) * mm, "end": v(-22.9, 15.24) * mm});
            skLineSegment(sketch, "E10.20.1", {"start": v(-24.41, 14.04) * mm, "end": v(-23.24, 13.77) * mm});
            skLineSegment(sketch, "E10.20.2", {"start": v(-22.9, 15.24) * mm, "end": v(-23.24, 13.77) * mm});
            skLineSegment(sketch, "E10.20.3", {"start": v(-22.1, 14.6) * mm, "end": v(-22.9, 15.24) * mm});
            skLineSegment(sketch, "E10.20.4", {"start": v(-22.22, 14) * mm, "end": v(-23.24, 13.77) * mm});
            skLineSegment(sketch, "E10.20.5", {"start": v(-24.08, 15.5) * mm, "end": v(-22.9, 15.24) * mm});
            skLineSegment(sketch, "E10.20.6", {"start": v(-23.24, 13.77) * mm, "end": v(-24.4, 14.04) * mm});
            skLineSegment(sketch, "E10.20.7", {"start": v(-22.9, 15.24) * mm, "end": v(-23.24, 13.77) * mm});
            skLineSegment(sketch, "E10.20.8", {"start": v(-22.08, 14.59) * mm, "end": v(-22.9, 15.24) * mm});
            skLineSegment(sketch, "E10.20.9", {"start": v(-22.21, 14) * mm, "end": v(-23.24, 13.77) * mm});
            skLineSegment(sketch, "E10.20.10", {"start": v(-24.24, 14.77) * mm, "end": v(-24.08, 15.5) * mm});
            skLineSegment(sketch, "E10.20.11", {"start": v(-24.08, 15.5) * mm, "end": v(-24.4, 14.04) * mm});
            skLineSegment(sketch, "E10.20.12", {"start": v(-24.24, 14.77) * mm, "end": v(-24.41, 14.04) * mm});
            skLineSegment(sketch, "E10.20.13", {"start": v(-22.08, 14.59) * mm, "end": v(-22.21, 14) * mm});
            skLineSegment(sketch, "E10.20.14", {"start": v(-22.16, 14.3) * mm, "end": v(-22.1, 14.6) * mm});
            skLineSegment(sketch, "E10.20.15", {"start": v(-22.16, 14.3) * mm, "end": v(-22.22, 14) * mm});
            skLineSegment(sketch, "E10.21.0", {"start": v(-23.92, 18.36) * mm, "end": v(-22.72, 18.36) * mm});
            skLineSegment(sketch, "E10.21.1", {"start": v(-23.92, 16.86) * mm, "end": v(-22.72, 16.86) * mm});
            skLineSegment(sketch, "E10.21.2", {"start": v(-22.72, 18.36) * mm, "end": v(-22.72, 16.86) * mm});
            skLineSegment(sketch, "E10.21.3", {"start": v(-21.78, 17.91) * mm, "end": v(-22.72, 18.36) * mm});
            skLineSegment(sketch, "E10.21.4", {"start": v(-21.78, 17.3) * mm, "end": v(-22.72, 16.86) * mm});
            skLineSegment(sketch, "E10.21.5", {"start": v(-23.92, 18.36) * mm, "end": v(-22.72, 18.36) * mm});
            skLineSegment(sketch, "E10.21.6", {"start": v(-22.72, 16.86) * mm, "end": v(-23.92, 16.86) * mm});
            skLineSegment(sketch, "E10.21.7", {"start": v(-22.72, 18.36) * mm, "end": v(-22.72, 16.86) * mm});
            skLineSegment(sketch, "E10.21.8", {"start": v(-21.77, 17.9) * mm, "end": v(-22.72, 18.36) * mm});
            skLineSegment(sketch, "E10.21.9", {"start": v(-21.77, 17.3) * mm, "end": v(-22.72, 16.86) * mm});
            skLineSegment(sketch, "E10.21.10", {"start": v(-23.92, 17.6) * mm, "end": v(-23.92, 18.36) * mm});
            skLineSegment(sketch, "E10.21.11", {"start": v(-23.92, 18.36) * mm, "end": v(-23.92, 16.86) * mm});
            skLineSegment(sketch, "E10.21.12", {"start": v(-23.92, 17.6) * mm, "end": v(-23.92, 16.86) * mm});
            skLineSegment(sketch, "E10.21.13", {"start": v(-21.77, 17.9) * mm, "end": v(-21.77, 17.3) * mm});
            skLineSegment(sketch, "E10.21.14", {"start": v(-21.78, 17.6) * mm, "end": v(-21.78, 17.91) * mm});
            skLineSegment(sketch, "E10.21.15", {"start": v(-21.78, 17.6) * mm, "end": v(-21.78, 17.3) * mm});
            skLineSegment(sketch, "E10.22.0", {"start": v(-24.41, 21.18) * mm, "end": v(-23.24, 21.44) * mm});
            skLineSegment(sketch, "E10.22.1", {"start": v(-24.08, 19.71) * mm, "end": v(-22.9, 19.98) * mm});
            skLineSegment(sketch, "E10.22.2", {"start": v(-23.24, 21.44) * mm, "end": v(-22.9, 19.98) * mm});
            skLineSegment(sketch, "E10.22.3", {"start": v(-22.23, 21.22) * mm, "end": v(-23.24, 21.44) * mm});
            skLineSegment(sketch, "E10.22.4", {"start": v(-22.1, 20.63) * mm, "end": v(-22.9, 19.98) * mm});
            skLineSegment(sketch, "E10.22.5", {"start": v(-24.4, 21.18) * mm, "end": v(-23.24, 21.44) * mm});
            skLineSegment(sketch, "E10.22.6", {"start": v(-22.9, 19.98) * mm, "end": v(-24.08, 19.72) * mm});
            skLineSegment(sketch, "E10.22.7", {"start": v(-23.24, 21.44) * mm, "end": v(-22.9, 19.98) * mm});
            skLineSegment(sketch, "E10.22.8", {"start": v(-22.21, 21.22) * mm, "end": v(-23.24, 21.44) * mm});
            skLineSegment(sketch, "E10.22.9", {"start": v(-22.08, 20.63) * mm, "end": v(-22.9, 19.98) * mm});
            skLineSegment(sketch, "E10.22.10", {"start": v(-24.24, 20.45) * mm, "end": v(-24.41, 21.18) * mm});
            skLineSegment(sketch, "E10.22.11", {"start": v(-24.4, 21.18) * mm, "end": v(-24.08, 19.72) * mm});
            skLineSegment(sketch, "E10.22.12", {"start": v(-24.24, 20.45) * mm, "end": v(-24.08, 19.71) * mm});
            skLineSegment(sketch, "E10.22.13", {"start": v(-22.21, 21.22) * mm, "end": v(-22.08, 20.63) * mm});
            skLineSegment(sketch, "E10.22.14", {"start": v(-22.16, 20.92) * mm, "end": v(-22.23, 21.22) * mm});
            skLineSegment(sketch, "E10.22.15", {"start": v(-22.16, 20.92) * mm, "end": v(-22.1, 20.63) * mm});
            skLineSegment(sketch, "E10.23.0", {"start": v(-25.51, 23.82) * mm, "end": v(-24.43, 24.34) * mm});
            skLineSegment(sketch, "E10.23.1", {"start": v(-24.86, 22.47) * mm, "end": v(-23.78, 22.99) * mm});
            skLineSegment(sketch, "E10.23.2", {"start": v(-24.43, 24.34) * mm, "end": v(-23.78, 22.99) * mm});
            skLineSegment(sketch, "E10.23.3", {"start": v(-23.4, 24.34) * mm, "end": v(-24.43, 24.34) * mm});
            skLineSegment(sketch, "E10.23.4", {"start": v(-23.13, 23.8) * mm, "end": v(-23.78, 22.99) * mm});
            skLineSegment(sketch, "E10.23.5", {"start": v(-25.51, 23.82) * mm, "end": v(-24.43, 24.34) * mm});
            skLineSegment(sketch, "E10.23.6", {"start": v(-23.78, 22.99) * mm, "end": v(-24.86, 22.47) * mm});
            skLineSegment(sketch, "E10.23.7", {"start": v(-24.43, 24.34) * mm, "end": v(-23.78, 22.99) * mm});
            skLineSegment(sketch, "E10.23.8", {"start": v(-23.38, 24.34) * mm, "end": v(-24.43, 24.34) * mm});
            skLineSegment(sketch, "E10.23.9", {"start": v(-23.12, 23.8) * mm, "end": v(-23.78, 22.99) * mm});
            skLineSegment(sketch, "E10.23.10", {"start": v(-25.19, 23.14) * mm, "end": v(-25.51, 23.82) * mm});
            skLineSegment(sketch, "E10.23.11", {"start": v(-25.51, 23.82) * mm, "end": v(-24.86, 22.47) * mm});
            skLineSegment(sketch, "E10.23.12", {"start": v(-25.19, 23.14) * mm, "end": v(-24.86, 22.47) * mm});
            skLineSegment(sketch, "E10.23.13", {"start": v(-23.38, 24.34) * mm, "end": v(-23.12, 23.8) * mm});
            skLineSegment(sketch, "E10.23.14", {"start": v(-23.26, 24.07) * mm, "end": v(-23.4, 24.34) * mm});
            skLineSegment(sketch, "E10.23.15", {"start": v(-23.26, 24.07) * mm, "end": v(-23.13, 23.8) * mm});
            skLineSegment(sketch, "E10.24.0", {"start": v(-27.17, 26.14) * mm, "end": v(-26.24, 26.9) * mm});
            skLineSegment(sketch, "E10.24.1", {"start": v(-26.24, 24.97) * mm, "end": v(-25.3, 25.72) * mm});
            skLineSegment(sketch, "E10.24.2", {"start": v(-26.24, 26.9) * mm, "end": v(-25.3, 25.72) * mm});
            skLineSegment(sketch, "E10.24.3", {"start": v(-25.22, 27.13) * mm, "end": v(-26.24, 26.9) * mm});
            skLineSegment(sketch, "E10.24.4", {"start": v(-24.85, 26.66) * mm, "end": v(-25.3, 25.72) * mm});
            skLineSegment(sketch, "E10.24.5", {"start": v(-27.17, 26.15) * mm, "end": v(-26.23, 26.9) * mm});
            skLineSegment(sketch, "E10.24.6", {"start": v(-25.3, 25.72) * mm, "end": v(-26.24, 24.97) * mm});
            skLineSegment(sketch, "E10.24.7", {"start": v(-26.23, 26.9) * mm, "end": v(-25.3, 25.72) * mm});
            skLineSegment(sketch, "E10.24.8", {"start": v(-25.21, 27.13) * mm, "end": v(-26.23, 26.9) * mm});
            skLineSegment(sketch, "E10.24.9", {"start": v(-24.84, 26.66) * mm, "end": v(-25.3, 25.72) * mm});
            skLineSegment(sketch, "E10.24.10", {"start": v(-26.7, 25.56) * mm, "end": v(-27.17, 26.14) * mm});
            skLineSegment(sketch, "E10.24.11", {"start": v(-27.17, 26.15) * mm, "end": v(-26.24, 24.97) * mm});
            skLineSegment(sketch, "E10.24.12", {"start": v(-26.7, 25.56) * mm, "end": v(-26.24, 24.97) * mm});
            skLineSegment(sketch, "E10.24.13", {"start": v(-25.21, 27.13) * mm, "end": v(-24.84, 26.66) * mm});
            skLineSegment(sketch, "E10.24.14", {"start": v(-25.03, 26.9) * mm, "end": v(-25.22, 27.13) * mm});
            skLineSegment(sketch, "E10.24.15", {"start": v(-25.03, 26.9) * mm, "end": v(-24.85, 26.66) * mm});
            skLineSegment(sketch, "E10.25.0", {"start": v(-29.31, 28.04) * mm, "end": v(-28.56, 28.98) * mm});
            skLineSegment(sketch, "E10.25.1", {"start": v(-28.14, 27.1) * mm, "end": v(-27.4, 28.05) * mm});
            skLineSegment(sketch, "E10.25.2", {"start": v(-28.56, 28.98) * mm, "end": v(-27.4, 28.05) * mm});
            skLineSegment(sketch, "E10.25.3", {"start": v(-27.63, 29.44) * mm, "end": v(-28.56, 28.98) * mm});
            skLineSegment(sketch, "E10.25.4", {"start": v(-27.16, 29.06) * mm, "end": v(-27.4, 28.05) * mm});
            skLineSegment(sketch, "E10.25.5", {"start": v(-29.31, 28.05) * mm, "end": v(-28.56, 28.98) * mm});
            skLineSegment(sketch, "E10.25.6", {"start": v(-27.39, 28.05) * mm, "end": v(-28.14, 27.11) * mm});
            skLineSegment(sketch, "E10.25.7", {"start": v(-28.56, 28.98) * mm, "end": v(-27.39, 28.05) * mm});
            skLineSegment(sketch, "E10.25.8", {"start": v(-27.62, 29.45) * mm, "end": v(-28.56, 28.98) * mm});
            skLineSegment(sketch, "E10.25.9", {"start": v(-27.15, 29.07) * mm, "end": v(-27.39, 28.05) * mm});
            skLineSegment(sketch, "E10.25.10", {"start": v(-28.73, 27.58) * mm, "end": v(-29.31, 28.04) * mm});
            skLineSegment(sketch, "E10.25.11", {"start": v(-29.31, 28.05) * mm, "end": v(-28.14, 27.11) * mm});
            skLineSegment(sketch, "E10.25.12", {"start": v(-28.73, 27.58) * mm, "end": v(-28.14, 27.1) * mm});
            skLineSegment(sketch, "E10.25.13", {"start": v(-27.62, 29.45) * mm, "end": v(-27.15, 29.07) * mm});
            skLineSegment(sketch, "E10.25.14", {"start": v(-27.4, 29.25) * mm, "end": v(-27.63, 29.44) * mm});
            skLineSegment(sketch, "E10.25.15", {"start": v(-27.4, 29.25) * mm, "end": v(-27.16, 29.06) * mm});
            skLineSegment(sketch, "E10.26.0", {"start": v(-31.82, 29.42) * mm, "end": v(-31.3, 30.5) * mm});
            skLineSegment(sketch, "E10.26.1", {"start": v(-30.47, 28.77) * mm, "end": v(-29.95, 29.85) * mm});
            skLineSegment(sketch, "E10.26.2", {"start": v(-31.3, 30.5) * mm, "end": v(-29.95, 29.85) * mm});
            skLineSegment(sketch, "E10.26.3", {"start": v(-30.49, 31.16) * mm, "end": v(-31.3, 30.5) * mm});
            skLineSegment(sketch, "E10.26.4", {"start": v(-29.94, 30.9) * mm, "end": v(-29.95, 29.85) * mm});
            skLineSegment(sketch, "E10.26.5", {"start": v(-31.82, 29.42) * mm, "end": v(-31.3, 30.5) * mm});
            skLineSegment(sketch, "E10.26.6", {"start": v(-29.95, 29.85) * mm, "end": v(-30.47, 28.77) * mm});
            skLineSegment(sketch, "E10.26.7", {"start": v(-31.3, 30.5) * mm, "end": v(-29.95, 29.85) * mm});
            skLineSegment(sketch, "E10.26.8", {"start": v(-30.48, 31.16) * mm, "end": v(-31.3, 30.5) * mm});
            skLineSegment(sketch, "E10.26.9", {"start": v(-29.94, 30.9) * mm, "end": v(-29.95, 29.85) * mm});
            skLineSegment(sketch, "E10.26.10", {"start": v(-31.14, 29.1) * mm, "end": v(-31.82, 29.42) * mm});
            skLineSegment(sketch, "E10.26.11", {"start": v(-31.82, 29.42) * mm, "end": v(-30.47, 28.77) * mm});
            skLineSegment(sketch, "E10.26.12", {"start": v(-31.14, 29.1) * mm, "end": v(-30.47, 28.77) * mm});
            skLineSegment(sketch, "E10.26.13", {"start": v(-30.48, 31.16) * mm, "end": v(-29.94, 30.9) * mm});
            skLineSegment(sketch, "E10.26.14", {"start": v(-30.21, 31.02) * mm, "end": v(-30.49, 31.16) * mm});
            skLineSegment(sketch, "E10.26.15", {"start": v(-30.21, 31.02) * mm, "end": v(-29.94, 30.9) * mm});
            skLineSegment(sketch, "E10.27.0", {"start": v(-34.57, 30.2) * mm, "end": v(-34.3, 31.38) * mm});
            skLineSegment(sketch, "E10.27.1", {"start": v(-33.1, 29.87) * mm, "end": v(-32.84, 31.04) * mm});
            skLineSegment(sketch, "E10.27.2", {"start": v(-34.3, 31.38) * mm, "end": v(-32.84, 31.04) * mm});
            skLineSegment(sketch, "E10.27.3", {"start": v(-33.66, 32.2) * mm, "end": v(-34.3, 31.38) * mm});
            skLineSegment(sketch, "E10.27.4", {"start": v(-33.07, 32.06) * mm, "end": v(-32.84, 31.04) * mm});
            skLineSegment(sketch, "E10.27.5", {"start": v(-34.57, 30.2) * mm, "end": v(-34.3, 31.38) * mm});
            skLineSegment(sketch, "E10.27.6", {"start": v(-32.84, 31.04) * mm, "end": v(-33.1, 29.87) * mm});
            skLineSegment(sketch, "E10.27.7", {"start": v(-34.3, 31.38) * mm, "end": v(-32.84, 31.04) * mm});
            skLineSegment(sketch, "E10.27.8", {"start": v(-33.65, 32.2) * mm, "end": v(-34.3, 31.38) * mm});
            skLineSegment(sketch, "E10.27.9", {"start": v(-33.07, 32.07) * mm, "end": v(-32.84, 31.04) * mm});
            skLineSegment(sketch, "E10.27.10", {"start": v(-33.84, 30.04) * mm, "end": v(-34.57, 30.2) * mm});
            skLineSegment(sketch, "E10.27.11", {"start": v(-34.57, 30.2) * mm, "end": v(-33.1, 29.87) * mm});
            skLineSegment(sketch, "E10.27.12", {"start": v(-33.84, 30.04) * mm, "end": v(-33.1, 29.87) * mm});
            skLineSegment(sketch, "E10.27.13", {"start": v(-33.65, 32.2) * mm, "end": v(-33.07, 32.07) * mm});
            skLineSegment(sketch, "E10.27.14", {"start": v(-33.36, 32.13) * mm, "end": v(-33.66, 32.2) * mm});
            skLineSegment(sketch, "E10.27.15", {"start": v(-33.36, 32.13) * mm, "end": v(-33.07, 32.06) * mm});
            skPoint(sketch, "E10.center", {"position": v(-36.67, 17.6) * mm});
            skCircle(sketch, "E11", {"center": v(-36.67, 17.6) * mm, "radius": 12.8 * mm});
            skSolve(sketch);
        }
        {
            var Q0;
            {var subQ0=sQuery(id+"F0.wireOp",EDGE,"E2");Q0=makeQuery(id+"F0.imprint","IMPRINT",FACE,{"disambiguationData":[TD([[makeQuery(id+"F0.imprint","IMPRINT",EDGE,{"derivedFrom":subQ0}),-1.0]])]});}
            var Q1;
            {var subQ0=sQuery(id+"F0.wireOp",EDGE,"E4");Q1=makeQuery(id+"F0.imprint","IMPRINT",FACE,{"disambiguationData":[TD([[makeQuery(id+"F0.imprint","IMPRINT",EDGE,{"derivedFrom":subQ0}),-1.0]])]});}
            var Q2;
            {var subQ0=sQuery(id+"F0.wireOp",EDGE,"E3");Q2=makeQuery(id+"F0.imprint","IMPRINT",FACE,{"disambiguationData":[TD([[makeQuery(id+"F0.imprint","IMPRINT",EDGE,{"derivedFrom":subQ0}),-1.0]])]});}
            var Q3;
            {var subQ0=sQuery(id+"F0.wireOp",EDGE,"E10.1.2");Q3=makeQuery(id+"F0.imprint","IMPRINT",FACE,{"disambiguationData":[TD([[makeQuery(id+"F0.imprint","IMPRINT",EDGE,{"derivedFrom":subQ0}),-1.0]])]});}
            var Q4;
            {var subQ1=sQuery(id+"F0.wireOp",EDGE,"E10.1.3");var subQ3=sQuery(id+"F0.wireOp",EDGE,"E10.1.7");var subQ4=makeQuery(id+"F0.imprint","INTERSECT",VERTEX,{"derivedFrom":[subQ1,subQ3]});Q4=makeQuery(id+"F0.imprint","IMPRINT",FACE,{"disambiguationData":[TD([[makeQuery(id+"F0.imprint","IMPRINT",EDGE,{"disambiguationData":[TD([[subQ4,-1.0]])],"derivedFrom":subQ1}),-1.0]])]});}
            var Q5;
            {var subQ1=sQuery(id+"F0.wireOp",EDGE,"E10.1.4");var subQ3=sQuery(id+"F0.wireOp",EDGE,"E10.1.7");var subQ4=makeQuery(id+"F0.imprint","INTERSECT",VERTEX,{"derivedFrom":[subQ1,subQ3]});Q5=makeQuery(id+"F0.imprint","IMPRINT",FACE,{"disambiguationData":[TD([[makeQuery(id+"F0.imprint","IMPRINT",EDGE,{"disambiguationData":[TD([[subQ4,-1.0]])],"derivedFrom":subQ1}),1.0]])]});}
            var Q6;
            {var subQ0=sQuery(id+"F0.wireOp",EDGE,"E10.2.2");Q6=makeQuery(id+"F0.imprint","IMPRINT",FACE,{"disambiguationData":[TD([[makeQuery(id+"F0.imprint","IMPRINT",EDGE,{"derivedFrom":subQ0}),-1.0]])]});}
            var Q7;
            {var subQ1=sQuery(id+"F0.wireOp",EDGE,"E10.2.3");var subQ3=sQuery(id+"F0.wireOp",EDGE,"E10.2.7");var subQ4=makeQuery(id+"F0.imprint","INTERSECT",VERTEX,{"derivedFrom":[subQ1,subQ3]});Q7=makeQuery(id+"F0.imprint","IMPRINT",FACE,{"disambiguationData":[TD([[makeQuery(id+"F0.imprint","IMPRINT",EDGE,{"disambiguationData":[TD([[subQ4,-1.0]])],"derivedFrom":subQ1}),-1.0]])]});}
            var Q8;
            {var subQ1=sQuery(id+"F0.wireOp",EDGE,"E10.2.4");var subQ3=sQuery(id+"F0.wireOp",EDGE,"E10.2.7");var subQ4=makeQuery(id+"F0.imprint","INTERSECT",VERTEX,{"derivedFrom":[subQ1,subQ3]});Q8=makeQuery(id+"F0.imprint","IMPRINT",FACE,{"disambiguationData":[TD([[makeQuery(id+"F0.imprint","IMPRINT",EDGE,{"disambiguationData":[TD([[subQ4,-1.0]])],"derivedFrom":subQ1}),1.0]])]});}
            var Q9;
            {var subQ0=sQuery(id+"F0.wireOp",EDGE,"E10.3.2");Q9=makeQuery(id+"F0.imprint","IMPRINT",FACE,{"disambiguationData":[TD([[makeQuery(id+"F0.imprint","IMPRINT",EDGE,{"derivedFrom":subQ0}),-1.0]])]});}
            var Q10;
            {var subQ1=sQuery(id+"F0.wireOp",EDGE,"E10.3.3");var subQ3=sQuery(id+"F0.wireOp",EDGE,"E10.3.7");var subQ4=makeQuery(id+"F0.imprint","INTERSECT",VERTEX,{"derivedFrom":[subQ1,subQ3]});Q10=makeQuery(id+"F0.imprint","IMPRINT",FACE,{"disambiguationData":[TD([[makeQuery(id+"F0.imprint","IMPRINT",EDGE,{"disambiguationData":[TD([[subQ4,-1.0]])],"derivedFrom":subQ1}),-1.0]])]});}
            var Q11;
            {var subQ1=sQuery(id+"F0.wireOp",EDGE,"E10.3.4");var subQ3=sQuery(id+"F0.wireOp",EDGE,"E10.3.7");var subQ4=makeQuery(id+"F0.imprint","INTERSECT",VERTEX,{"derivedFrom":[subQ1,subQ3]});Q11=makeQuery(id+"F0.imprint","IMPRINT",FACE,{"disambiguationData":[TD([[makeQuery(id+"F0.imprint","IMPRINT",EDGE,{"disambiguationData":[TD([[subQ4,-1.0]])],"derivedFrom":subQ1}),1.0]])]});}
            var Q12;
            {var subQ0=sQuery(id+"F0.wireOp",EDGE,"E10.4.2");Q12=makeQuery(id+"F0.imprint","IMPRINT",FACE,{"disambiguationData":[TD([[makeQuery(id+"F0.imprint","IMPRINT",EDGE,{"derivedFrom":subQ0}),-1.0]])]});}
            var Q13;
            {var subQ1=sQuery(id+"F0.wireOp",EDGE,"E10.4.3");var subQ3=sQuery(id+"F0.wireOp",EDGE,"E10.4.7");var subQ4=makeQuery(id+"F0.imprint","INTERSECT",VERTEX,{"derivedFrom":[subQ1,subQ3]});Q13=makeQuery(id+"F0.imprint","IMPRINT",FACE,{"disambiguationData":[TD([[makeQuery(id+"F0.imprint","IMPRINT",EDGE,{"disambiguationData":[TD([[subQ4,-1.0]])],"derivedFrom":subQ1}),-1.0]])]});}
            var Q14;
            {var subQ1=sQuery(id+"F0.wireOp",EDGE,"E10.4.4");var subQ3=sQuery(id+"F0.wireOp",EDGE,"E10.4.7");var subQ4=makeQuery(id+"F0.imprint","INTERSECT",VERTEX,{"derivedFrom":[subQ1,subQ3]});Q14=makeQuery(id+"F0.imprint","IMPRINT",FACE,{"disambiguationData":[TD([[makeQuery(id+"F0.imprint","IMPRINT",EDGE,{"disambiguationData":[TD([[subQ4,-1.0]])],"derivedFrom":subQ1}),1.0]])]});}
            var Q15;
            {var subQ0=sQuery(id+"F0.wireOp",EDGE,"E10.5.2");Q15=makeQuery(id+"F0.imprint","IMPRINT",FACE,{"disambiguationData":[TD([[makeQuery(id+"F0.imprint","IMPRINT",EDGE,{"derivedFrom":subQ0}),-1.0]])]});}
            var Q16;
            {var subQ1=sQuery(id+"F0.wireOp",EDGE,"E10.5.3");var subQ3=sQuery(id+"F0.wireOp",EDGE,"E10.5.7");var subQ4=makeQuery(id+"F0.imprint","INTERSECT",VERTEX,{"derivedFrom":[subQ1,subQ3]});Q16=makeQuery(id+"F0.imprint","IMPRINT",FACE,{"disambiguationData":[TD([[makeQuery(id+"F0.imprint","IMPRINT",EDGE,{"disambiguationData":[TD([[subQ4,-1.0]])],"derivedFrom":subQ1}),-1.0]])]});}
            var Q17;
            {var subQ1=sQuery(id+"F0.wireOp",EDGE,"E10.5.4");var subQ3=sQuery(id+"F0.wireOp",EDGE,"E10.5.7");var subQ4=makeQuery(id+"F0.imprint","INTERSECT",VERTEX,{"derivedFrom":[subQ1,subQ3]});Q17=makeQuery(id+"F0.imprint","IMPRINT",FACE,{"disambiguationData":[TD([[makeQuery(id+"F0.imprint","IMPRINT",EDGE,{"disambiguationData":[TD([[subQ4,-1.0]])],"derivedFrom":subQ1}),1.0]])]});}
            var Q18;
            {var subQ0=sQuery(id+"F0.wireOp",EDGE,"E10.6.2");Q18=makeQuery(id+"F0.imprint","IMPRINT",FACE,{"disambiguationData":[TD([[makeQuery(id+"F0.imprint","IMPRINT",EDGE,{"derivedFrom":subQ0}),-1.0]])]});}
            var Q19;
            {var subQ1=sQuery(id+"F0.wireOp",EDGE,"E10.6.3");var subQ3=sQuery(id+"F0.wireOp",EDGE,"E10.6.7");var subQ4=makeQuery(id+"F0.imprint","INTERSECT",VERTEX,{"derivedFrom":[subQ1,subQ3]});Q19=makeQuery(id+"F0.imprint","IMPRINT",FACE,{"disambiguationData":[TD([[makeQuery(id+"F0.imprint","IMPRINT",EDGE,{"disambiguationData":[TD([[subQ4,-1.0]])],"derivedFrom":subQ1}),-1.0]])]});}
            var Q20;
            {var subQ1=sQuery(id+"F0.wireOp",EDGE,"E10.6.4");var subQ3=sQuery(id+"F0.wireOp",EDGE,"E10.6.7");var subQ4=makeQuery(id+"F0.imprint","INTERSECT",VERTEX,{"derivedFrom":[subQ1,subQ3]});Q20=makeQuery(id+"F0.imprint","IMPRINT",FACE,{"disambiguationData":[TD([[makeQuery(id+"F0.imprint","IMPRINT",EDGE,{"disambiguationData":[TD([[subQ4,-1.0]])],"derivedFrom":subQ1}),1.0]])]});}
            var Q21;
            {var subQ0=sQuery(id+"F0.wireOp",EDGE,"E10.7.2");Q21=makeQuery(id+"F0.imprint","IMPRINT",FACE,{"disambiguationData":[TD([[makeQuery(id+"F0.imprint","IMPRINT",EDGE,{"derivedFrom":subQ0}),-1.0]])]});}
            var Q22;
            {var subQ1=sQuery(id+"F0.wireOp",EDGE,"E10.7.3");var subQ3=sQuery(id+"F0.wireOp",EDGE,"E10.7.7");var subQ4=makeQuery(id+"F0.imprint","INTERSECT",VERTEX,{"derivedFrom":[subQ1,subQ3]});Q22=makeQuery(id+"F0.imprint","IMPRINT",FACE,{"disambiguationData":[TD([[makeQuery(id+"F0.imprint","IMPRINT",EDGE,{"disambiguationData":[TD([[subQ4,-1.0]])],"derivedFrom":subQ1}),-1.0]])]});}
            var Q23;
            {var subQ1=sQuery(id+"F0.wireOp",EDGE,"E10.7.4");var subQ3=sQuery(id+"F0.wireOp",EDGE,"E10.7.7");var subQ4=makeQuery(id+"F0.imprint","INTERSECT",VERTEX,{"derivedFrom":[subQ1,subQ3]});Q23=makeQuery(id+"F0.imprint","IMPRINT",FACE,{"disambiguationData":[TD([[makeQuery(id+"F0.imprint","IMPRINT",EDGE,{"disambiguationData":[TD([[subQ4,-1.0]])],"derivedFrom":subQ1}),1.0]])]});}
            var Q24;
            {var subQ0=sQuery(id+"F0.wireOp",EDGE,"E10.8.2");Q24=makeQuery(id+"F0.imprint","IMPRINT",FACE,{"disambiguationData":[TD([[makeQuery(id+"F0.imprint","IMPRINT",EDGE,{"derivedFrom":subQ0}),-1.0]])]});}
            var Q25;
            {var subQ1=sQuery(id+"F0.wireOp",EDGE,"E10.8.3");var subQ3=sQuery(id+"F0.wireOp",EDGE,"E10.8.7");var subQ4=makeQuery(id+"F0.imprint","INTERSECT",VERTEX,{"derivedFrom":[subQ1,subQ3]});Q25=makeQuery(id+"F0.imprint","IMPRINT",FACE,{"disambiguationData":[TD([[makeQuery(id+"F0.imprint","IMPRINT",EDGE,{"disambiguationData":[TD([[subQ4,-1.0]])],"derivedFrom":subQ1}),-1.0]])]});}
            var Q26;
            {var subQ1=sQuery(id+"F0.wireOp",EDGE,"E10.8.4");var subQ3=sQuery(id+"F0.wireOp",EDGE,"E10.8.7");var subQ4=makeQuery(id+"F0.imprint","INTERSECT",VERTEX,{"derivedFrom":[subQ1,subQ3]});Q26=makeQuery(id+"F0.imprint","IMPRINT",FACE,{"disambiguationData":[TD([[makeQuery(id+"F0.imprint","IMPRINT",EDGE,{"disambiguationData":[TD([[subQ4,-1.0]])],"derivedFrom":subQ1}),1.0]])]});}
            var Q27;
            {var subQ0=sQuery(id+"F0.wireOp",EDGE,"E10.9.2");Q27=makeQuery(id+"F0.imprint","IMPRINT",FACE,{"disambiguationData":[TD([[makeQuery(id+"F0.imprint","IMPRINT",EDGE,{"derivedFrom":subQ0}),-1.0]])]});}
            var Q28;
            {var subQ1=sQuery(id+"F0.wireOp",EDGE,"E10.9.3");var subQ3=sQuery(id+"F0.wireOp",EDGE,"E10.9.7");var subQ4=makeQuery(id+"F0.imprint","INTERSECT",VERTEX,{"derivedFrom":[subQ1,subQ3]});Q28=makeQuery(id+"F0.imprint","IMPRINT",FACE,{"disambiguationData":[TD([[makeQuery(id+"F0.imprint","IMPRINT",EDGE,{"disambiguationData":[TD([[subQ4,-1.0]])],"derivedFrom":subQ1}),-1.0]])]});}
            var Q29;
            {var subQ1=sQuery(id+"F0.wireOp",EDGE,"E10.9.4");var subQ3=sQuery(id+"F0.wireOp",EDGE,"E10.9.7");var subQ4=makeQuery(id+"F0.imprint","INTERSECT",VERTEX,{"derivedFrom":[subQ1,subQ3]});Q29=makeQuery(id+"F0.imprint","IMPRINT",FACE,{"disambiguationData":[TD([[makeQuery(id+"F0.imprint","IMPRINT",EDGE,{"disambiguationData":[TD([[subQ4,-1.0]])],"derivedFrom":subQ1}),1.0]])]});}
            var Q30;
            {var subQ0=sQuery(id+"F0.wireOp",EDGE,"E10.10.2");Q30=makeQuery(id+"F0.imprint","IMPRINT",FACE,{"disambiguationData":[TD([[makeQuery(id+"F0.imprint","IMPRINT",EDGE,{"derivedFrom":subQ0}),-1.0]])]});}
            var Q31;
            {var subQ1=sQuery(id+"F0.wireOp",EDGE,"E10.10.3");var subQ3=sQuery(id+"F0.wireOp",EDGE,"E10.10.7");var subQ4=makeQuery(id+"F0.imprint","INTERSECT",VERTEX,{"derivedFrom":[subQ1,subQ3]});Q31=makeQuery(id+"F0.imprint","IMPRINT",FACE,{"disambiguationData":[TD([[makeQuery(id+"F0.imprint","IMPRINT",EDGE,{"disambiguationData":[TD([[subQ4,-1.0]])],"derivedFrom":subQ1}),-1.0]])]});}
            var Q32;
            {var subQ1=sQuery(id+"F0.wireOp",EDGE,"E10.10.4");var subQ3=sQuery(id+"F0.wireOp",EDGE,"E10.10.7");var subQ4=makeQuery(id+"F0.imprint","INTERSECT",VERTEX,{"derivedFrom":[subQ1,subQ3]});Q32=makeQuery(id+"F0.imprint","IMPRINT",FACE,{"disambiguationData":[TD([[makeQuery(id+"F0.imprint","IMPRINT",EDGE,{"disambiguationData":[TD([[subQ4,-1.0]])],"derivedFrom":subQ1}),1.0]])]});}
            var Q33;
            {var subQ0=sQuery(id+"F0.wireOp",EDGE,"E10.11.2");Q33=makeQuery(id+"F0.imprint","IMPRINT",FACE,{"disambiguationData":[TD([[makeQuery(id+"F0.imprint","IMPRINT",EDGE,{"derivedFrom":subQ0}),-1.0]])]});}
            var Q34;
            {var subQ1=sQuery(id+"F0.wireOp",EDGE,"E10.11.3");var subQ3=sQuery(id+"F0.wireOp",EDGE,"E10.11.7");var subQ4=makeQuery(id+"F0.imprint","INTERSECT",VERTEX,{"derivedFrom":[subQ1,subQ3]});Q34=makeQuery(id+"F0.imprint","IMPRINT",FACE,{"disambiguationData":[TD([[makeQuery(id+"F0.imprint","IMPRINT",EDGE,{"disambiguationData":[TD([[subQ4,-1.0]])],"derivedFrom":subQ1}),-1.0]])]});}
            var Q35;
            {var subQ1=sQuery(id+"F0.wireOp",EDGE,"E10.11.4");var subQ3=sQuery(id+"F0.wireOp",EDGE,"E10.11.7");var subQ4=makeQuery(id+"F0.imprint","INTERSECT",VERTEX,{"derivedFrom":[subQ1,subQ3]});Q35=makeQuery(id+"F0.imprint","IMPRINT",FACE,{"disambiguationData":[TD([[makeQuery(id+"F0.imprint","IMPRINT",EDGE,{"disambiguationData":[TD([[subQ4,-1.0]])],"derivedFrom":subQ1}),1.0]])]});}
            var Q36;
            {var subQ0=sQuery(id+"F0.wireOp",EDGE,"E10.12.2");Q36=makeQuery(id+"F0.imprint","IMPRINT",FACE,{"disambiguationData":[TD([[makeQuery(id+"F0.imprint","IMPRINT",EDGE,{"derivedFrom":subQ0}),-1.0]])]});}
            var Q37;
            {var subQ1=sQuery(id+"F0.wireOp",EDGE,"E10.12.3");var subQ3=sQuery(id+"F0.wireOp",EDGE,"E10.12.7");var subQ4=makeQuery(id+"F0.imprint","INTERSECT",VERTEX,{"derivedFrom":[subQ1,subQ3]});Q37=makeQuery(id+"F0.imprint","IMPRINT",FACE,{"disambiguationData":[TD([[makeQuery(id+"F0.imprint","IMPRINT",EDGE,{"disambiguationData":[TD([[subQ4,-1.0]])],"derivedFrom":subQ1}),-1.0]])]});}
            var Q38;
            {var subQ1=sQuery(id+"F0.wireOp",EDGE,"E10.12.4");var subQ3=sQuery(id+"F0.wireOp",EDGE,"E10.12.7");var subQ4=makeQuery(id+"F0.imprint","INTERSECT",VERTEX,{"derivedFrom":[subQ1,subQ3]});Q38=makeQuery(id+"F0.imprint","IMPRINT",FACE,{"disambiguationData":[TD([[makeQuery(id+"F0.imprint","IMPRINT",EDGE,{"disambiguationData":[TD([[subQ4,-1.0]])],"derivedFrom":subQ1}),1.0]])]});}
            var Q39;
            {var subQ0=sQuery(id+"F0.wireOp",EDGE,"E10.13.2");Q39=makeQuery(id+"F0.imprint","IMPRINT",FACE,{"disambiguationData":[TD([[makeQuery(id+"F0.imprint","IMPRINT",EDGE,{"derivedFrom":subQ0}),-1.0]])]});}
            var Q40;
            {var subQ1=sQuery(id+"F0.wireOp",EDGE,"E10.13.3");var subQ3=sQuery(id+"F0.wireOp",EDGE,"E10.13.7");var subQ4=makeQuery(id+"F0.imprint","INTERSECT",VERTEX,{"derivedFrom":[subQ1,subQ3]});Q40=makeQuery(id+"F0.imprint","IMPRINT",FACE,{"disambiguationData":[TD([[makeQuery(id+"F0.imprint","IMPRINT",EDGE,{"disambiguationData":[TD([[subQ4,-1.0]])],"derivedFrom":subQ1}),-1.0]])]});}
            var Q41;
            {var subQ1=sQuery(id+"F0.wireOp",EDGE,"E10.13.4");var subQ3=sQuery(id+"F0.wireOp",EDGE,"E10.13.7");var subQ4=makeQuery(id+"F0.imprint","INTERSECT",VERTEX,{"derivedFrom":[subQ1,subQ3]});Q41=makeQuery(id+"F0.imprint","IMPRINT",FACE,{"disambiguationData":[TD([[makeQuery(id+"F0.imprint","IMPRINT",EDGE,{"disambiguationData":[TD([[subQ4,-1.0]])],"derivedFrom":subQ1}),1.0]])]});}
            var Q42;
            {var subQ0=sQuery(id+"F0.wireOp",EDGE,"E10.14.2");Q42=makeQuery(id+"F0.imprint","IMPRINT",FACE,{"disambiguationData":[TD([[makeQuery(id+"F0.imprint","IMPRINT",EDGE,{"derivedFrom":subQ0}),-1.0]])]});}
            var Q43;
            {var subQ1=sQuery(id+"F0.wireOp",EDGE,"E10.14.3");var subQ3=sQuery(id+"F0.wireOp",EDGE,"E10.14.7");var subQ4=makeQuery(id+"F0.imprint","INTERSECT",VERTEX,{"derivedFrom":[subQ1,subQ3]});Q43=makeQuery(id+"F0.imprint","IMPRINT",FACE,{"disambiguationData":[TD([[makeQuery(id+"F0.imprint","IMPRINT",EDGE,{"disambiguationData":[TD([[subQ4,-1.0]])],"derivedFrom":subQ1}),-1.0]])]});}
            var Q44;
            {var subQ1=sQuery(id+"F0.wireOp",EDGE,"E10.14.4");var subQ3=sQuery(id+"F0.wireOp",EDGE,"E10.14.7");var subQ4=makeQuery(id+"F0.imprint","INTERSECT",VERTEX,{"derivedFrom":[subQ1,subQ3]});Q44=makeQuery(id+"F0.imprint","IMPRINT",FACE,{"disambiguationData":[TD([[makeQuery(id+"F0.imprint","IMPRINT",EDGE,{"disambiguationData":[TD([[subQ4,-1.0]])],"derivedFrom":subQ1}),1.0]])]});}
            var Q45;
            {var subQ0=sQuery(id+"F0.wireOp",EDGE,"E10.15.2");Q45=makeQuery(id+"F0.imprint","IMPRINT",FACE,{"disambiguationData":[TD([[makeQuery(id+"F0.imprint","IMPRINT",EDGE,{"derivedFrom":subQ0}),-1.0]])]});}
            var Q46;
            {var subQ1=sQuery(id+"F0.wireOp",EDGE,"E10.15.3");var subQ3=sQuery(id+"F0.wireOp",EDGE,"E10.15.7");var subQ4=makeQuery(id+"F0.imprint","INTERSECT",VERTEX,{"derivedFrom":[subQ1,subQ3]});Q46=makeQuery(id+"F0.imprint","IMPRINT",FACE,{"disambiguationData":[TD([[makeQuery(id+"F0.imprint","IMPRINT",EDGE,{"disambiguationData":[TD([[subQ4,-1.0]])],"derivedFrom":subQ1}),-1.0]])]});}
            var Q47;
            {var subQ1=sQuery(id+"F0.wireOp",EDGE,"E10.15.4");var subQ3=sQuery(id+"F0.wireOp",EDGE,"E10.15.7");var subQ4=makeQuery(id+"F0.imprint","INTERSECT",VERTEX,{"derivedFrom":[subQ1,subQ3]});Q47=makeQuery(id+"F0.imprint","IMPRINT",FACE,{"disambiguationData":[TD([[makeQuery(id+"F0.imprint","IMPRINT",EDGE,{"disambiguationData":[TD([[subQ4,-1.0]])],"derivedFrom":subQ1}),1.0]])]});}
            var Q48;
            {var subQ0=sQuery(id+"F0.wireOp",EDGE,"E10.16.2");Q48=makeQuery(id+"F0.imprint","IMPRINT",FACE,{"disambiguationData":[TD([[makeQuery(id+"F0.imprint","IMPRINT",EDGE,{"derivedFrom":subQ0}),-1.0]])]});}
            var Q49;
            {var subQ1=sQuery(id+"F0.wireOp",EDGE,"E10.16.3");var subQ3=sQuery(id+"F0.wireOp",EDGE,"E10.16.7");var subQ4=makeQuery(id+"F0.imprint","INTERSECT",VERTEX,{"derivedFrom":[subQ1,subQ3]});Q49=makeQuery(id+"F0.imprint","IMPRINT",FACE,{"disambiguationData":[TD([[makeQuery(id+"F0.imprint","IMPRINT",EDGE,{"disambiguationData":[TD([[subQ4,-1.0]])],"derivedFrom":subQ1}),-1.0]])]});}
            var Q50;
            {var subQ1=sQuery(id+"F0.wireOp",EDGE,"E10.16.4");var subQ3=sQuery(id+"F0.wireOp",EDGE,"E10.16.7");var subQ4=makeQuery(id+"F0.imprint","INTERSECT",VERTEX,{"derivedFrom":[subQ1,subQ3]});Q50=makeQuery(id+"F0.imprint","IMPRINT",FACE,{"disambiguationData":[TD([[makeQuery(id+"F0.imprint","IMPRINT",EDGE,{"disambiguationData":[TD([[subQ4,-1.0]])],"derivedFrom":subQ1}),1.0]])]});}
            var Q51;
            {var subQ0=sQuery(id+"F0.wireOp",EDGE,"E10.17.2");Q51=makeQuery(id+"F0.imprint","IMPRINT",FACE,{"disambiguationData":[TD([[makeQuery(id+"F0.imprint","IMPRINT",EDGE,{"derivedFrom":subQ0}),-1.0]])]});}
            var Q52;
            {var subQ1=sQuery(id+"F0.wireOp",EDGE,"E10.17.3");var subQ3=sQuery(id+"F0.wireOp",EDGE,"E10.17.7");var subQ4=makeQuery(id+"F0.imprint","INTERSECT",VERTEX,{"derivedFrom":[subQ1,subQ3]});Q52=makeQuery(id+"F0.imprint","IMPRINT",FACE,{"disambiguationData":[TD([[makeQuery(id+"F0.imprint","IMPRINT",EDGE,{"disambiguationData":[TD([[subQ4,-1.0]])],"derivedFrom":subQ1}),-1.0]])]});}
            var Q53;
            {var subQ1=sQuery(id+"F0.wireOp",EDGE,"E10.17.4");var subQ3=sQuery(id+"F0.wireOp",EDGE,"E10.17.7");var subQ4=makeQuery(id+"F0.imprint","INTERSECT",VERTEX,{"derivedFrom":[subQ1,subQ3]});Q53=makeQuery(id+"F0.imprint","IMPRINT",FACE,{"disambiguationData":[TD([[makeQuery(id+"F0.imprint","IMPRINT",EDGE,{"disambiguationData":[TD([[subQ4,-1.0]])],"derivedFrom":subQ1}),1.0]])]});}
            var Q54;
            {var subQ0=sQuery(id+"F0.wireOp",EDGE,"E10.18.2");Q54=makeQuery(id+"F0.imprint","IMPRINT",FACE,{"disambiguationData":[TD([[makeQuery(id+"F0.imprint","IMPRINT",EDGE,{"derivedFrom":subQ0}),-1.0]])]});}
            var Q55;
            {var subQ1=sQuery(id+"F0.wireOp",EDGE,"E10.18.3");var subQ3=sQuery(id+"F0.wireOp",EDGE,"E10.18.7");var subQ4=makeQuery(id+"F0.imprint","INTERSECT",VERTEX,{"derivedFrom":[subQ1,subQ3]});Q55=makeQuery(id+"F0.imprint","IMPRINT",FACE,{"disambiguationData":[TD([[makeQuery(id+"F0.imprint","IMPRINT",EDGE,{"disambiguationData":[TD([[subQ4,-1.0]])],"derivedFrom":subQ1}),-1.0]])]});}
            var Q56;
            {var subQ1=sQuery(id+"F0.wireOp",EDGE,"E10.18.4");var subQ3=sQuery(id+"F0.wireOp",EDGE,"E10.18.7");var subQ4=makeQuery(id+"F0.imprint","INTERSECT",VERTEX,{"derivedFrom":[subQ1,subQ3]});Q56=makeQuery(id+"F0.imprint","IMPRINT",FACE,{"disambiguationData":[TD([[makeQuery(id+"F0.imprint","IMPRINT",EDGE,{"disambiguationData":[TD([[subQ4,-1.0]])],"derivedFrom":subQ1}),1.0]])]});}
            var Q57;
            {var subQ0=sQuery(id+"F0.wireOp",EDGE,"E10.19.2");Q57=makeQuery(id+"F0.imprint","IMPRINT",FACE,{"disambiguationData":[TD([[makeQuery(id+"F0.imprint","IMPRINT",EDGE,{"derivedFrom":subQ0}),-1.0]])]});}
            var Q58;
            {var subQ1=sQuery(id+"F0.wireOp",EDGE,"E10.19.3");var subQ3=sQuery(id+"F0.wireOp",EDGE,"E10.19.7");var subQ4=makeQuery(id+"F0.imprint","INTERSECT",VERTEX,{"derivedFrom":[subQ1,subQ3]});Q58=makeQuery(id+"F0.imprint","IMPRINT",FACE,{"disambiguationData":[TD([[makeQuery(id+"F0.imprint","IMPRINT",EDGE,{"disambiguationData":[TD([[subQ4,-1.0]])],"derivedFrom":subQ1}),-1.0]])]});}
            var Q59;
            {var subQ1=sQuery(id+"F0.wireOp",EDGE,"E10.19.4");var subQ3=sQuery(id+"F0.wireOp",EDGE,"E10.19.7");var subQ4=makeQuery(id+"F0.imprint","INTERSECT",VERTEX,{"derivedFrom":[subQ1,subQ3]});Q59=makeQuery(id+"F0.imprint","IMPRINT",FACE,{"disambiguationData":[TD([[makeQuery(id+"F0.imprint","IMPRINT",EDGE,{"disambiguationData":[TD([[subQ4,-1.0]])],"derivedFrom":subQ1}),1.0]])]});}
            var Q60;
            {var subQ0=sQuery(id+"F0.wireOp",EDGE,"E10.20.2");Q60=makeQuery(id+"F0.imprint","IMPRINT",FACE,{"disambiguationData":[TD([[makeQuery(id+"F0.imprint","IMPRINT",EDGE,{"derivedFrom":subQ0}),-1.0]])]});}
            var Q61;
            {var subQ1=sQuery(id+"F0.wireOp",EDGE,"E10.20.3");var subQ3=sQuery(id+"F0.wireOp",EDGE,"E10.20.7");var subQ4=makeQuery(id+"F0.imprint","INTERSECT",VERTEX,{"derivedFrom":[subQ1,subQ3]});Q61=makeQuery(id+"F0.imprint","IMPRINT",FACE,{"disambiguationData":[TD([[makeQuery(id+"F0.imprint","IMPRINT",EDGE,{"disambiguationData":[TD([[subQ4,-1.0]])],"derivedFrom":subQ1}),-1.0]])]});}
            var Q62;
            {var subQ1=sQuery(id+"F0.wireOp",EDGE,"E10.20.4");var subQ3=sQuery(id+"F0.wireOp",EDGE,"E10.20.7");var subQ4=makeQuery(id+"F0.imprint","INTERSECT",VERTEX,{"derivedFrom":[subQ1,subQ3]});Q62=makeQuery(id+"F0.imprint","IMPRINT",FACE,{"disambiguationData":[TD([[makeQuery(id+"F0.imprint","IMPRINT",EDGE,{"disambiguationData":[TD([[subQ4,-1.0]])],"derivedFrom":subQ1}),1.0]])]});}
            var Q63;
            {var subQ0=sQuery(id+"F0.wireOp",EDGE,"E10.21.2");Q63=makeQuery(id+"F0.imprint","IMPRINT",FACE,{"disambiguationData":[TD([[makeQuery(id+"F0.imprint","IMPRINT",EDGE,{"derivedFrom":subQ0}),-1.0]])]});}
            var Q64;
            {var subQ1=sQuery(id+"F0.wireOp",EDGE,"E10.21.3");var subQ3=sQuery(id+"F0.wireOp",EDGE,"E10.21.7");var subQ4=makeQuery(id+"F0.imprint","INTERSECT",VERTEX,{"derivedFrom":[subQ1,subQ3]});Q64=makeQuery(id+"F0.imprint","IMPRINT",FACE,{"disambiguationData":[TD([[makeQuery(id+"F0.imprint","IMPRINT",EDGE,{"disambiguationData":[TD([[subQ4,-1.0]])],"derivedFrom":subQ1}),-1.0]])]});}
            var Q65;
            {var subQ1=sQuery(id+"F0.wireOp",EDGE,"E10.21.4");var subQ3=sQuery(id+"F0.wireOp",EDGE,"E10.21.7");var subQ4=makeQuery(id+"F0.imprint","INTERSECT",VERTEX,{"derivedFrom":[subQ1,subQ3]});Q65=makeQuery(id+"F0.imprint","IMPRINT",FACE,{"disambiguationData":[TD([[makeQuery(id+"F0.imprint","IMPRINT",EDGE,{"disambiguationData":[TD([[subQ4,-1.0]])],"derivedFrom":subQ1}),1.0]])]});}
            var Q66;
            {var subQ0=sQuery(id+"F0.wireOp",EDGE,"E10.22.2");Q66=makeQuery(id+"F0.imprint","IMPRINT",FACE,{"disambiguationData":[TD([[makeQuery(id+"F0.imprint","IMPRINT",EDGE,{"derivedFrom":subQ0}),-1.0]])]});}
            var Q67;
            {var subQ1=sQuery(id+"F0.wireOp",EDGE,"E10.22.3");var subQ3=sQuery(id+"F0.wireOp",EDGE,"E10.22.7");var subQ4=makeQuery(id+"F0.imprint","INTERSECT",VERTEX,{"derivedFrom":[subQ1,subQ3]});Q67=makeQuery(id+"F0.imprint","IMPRINT",FACE,{"disambiguationData":[TD([[makeQuery(id+"F0.imprint","IMPRINT",EDGE,{"disambiguationData":[TD([[subQ4,-1.0]])],"derivedFrom":subQ1}),-1.0]])]});}
            var Q68;
            {var subQ1=sQuery(id+"F0.wireOp",EDGE,"E10.22.4");var subQ3=sQuery(id+"F0.wireOp",EDGE,"E10.22.7");var subQ4=makeQuery(id+"F0.imprint","INTERSECT",VERTEX,{"derivedFrom":[subQ1,subQ3]});Q68=makeQuery(id+"F0.imprint","IMPRINT",FACE,{"disambiguationData":[TD([[makeQuery(id+"F0.imprint","IMPRINT",EDGE,{"disambiguationData":[TD([[subQ4,-1.0]])],"derivedFrom":subQ1}),1.0]])]});}
            var Q69;
            {var subQ0=sQuery(id+"F0.wireOp",EDGE,"E10.23.2");Q69=makeQuery(id+"F0.imprint","IMPRINT",FACE,{"disambiguationData":[TD([[makeQuery(id+"F0.imprint","IMPRINT",EDGE,{"derivedFrom":subQ0}),-1.0]])]});}
            var Q70;
            {var subQ1=sQuery(id+"F0.wireOp",EDGE,"E10.23.3");var subQ3=sQuery(id+"F0.wireOp",EDGE,"E10.23.7");var subQ4=makeQuery(id+"F0.imprint","INTERSECT",VERTEX,{"derivedFrom":[subQ1,subQ3]});Q70=makeQuery(id+"F0.imprint","IMPRINT",FACE,{"disambiguationData":[TD([[makeQuery(id+"F0.imprint","IMPRINT",EDGE,{"disambiguationData":[TD([[subQ4,-1.0]])],"derivedFrom":subQ1}),-1.0]])]});}
            var Q71;
            {var subQ1=sQuery(id+"F0.wireOp",EDGE,"E10.23.4");var subQ3=sQuery(id+"F0.wireOp",EDGE,"E10.23.7");var subQ4=makeQuery(id+"F0.imprint","INTERSECT",VERTEX,{"derivedFrom":[subQ1,subQ3]});Q71=makeQuery(id+"F0.imprint","IMPRINT",FACE,{"disambiguationData":[TD([[makeQuery(id+"F0.imprint","IMPRINT",EDGE,{"disambiguationData":[TD([[subQ4,-1.0]])],"derivedFrom":subQ1}),1.0]])]});}
            var Q72;
            {var subQ0=sQuery(id+"F0.wireOp",EDGE,"E10.24.2");Q72=makeQuery(id+"F0.imprint","IMPRINT",FACE,{"disambiguationData":[TD([[makeQuery(id+"F0.imprint","IMPRINT",EDGE,{"derivedFrom":subQ0}),-1.0]])]});}
            var Q73;
            {var subQ1=sQuery(id+"F0.wireOp",EDGE,"E10.24.3");var subQ3=sQuery(id+"F0.wireOp",EDGE,"E10.24.7");var subQ4=makeQuery(id+"F0.imprint","INTERSECT",VERTEX,{"derivedFrom":[subQ1,subQ3]});Q73=makeQuery(id+"F0.imprint","IMPRINT",FACE,{"disambiguationData":[TD([[makeQuery(id+"F0.imprint","IMPRINT",EDGE,{"disambiguationData":[TD([[subQ4,-1.0]])],"derivedFrom":subQ1}),-1.0]])]});}
            var Q74;
            {var subQ1=sQuery(id+"F0.wireOp",EDGE,"E10.24.4");var subQ3=sQuery(id+"F0.wireOp",EDGE,"E10.24.7");var subQ4=makeQuery(id+"F0.imprint","INTERSECT",VERTEX,{"derivedFrom":[subQ1,subQ3]});Q74=makeQuery(id+"F0.imprint","IMPRINT",FACE,{"disambiguationData":[TD([[makeQuery(id+"F0.imprint","IMPRINT",EDGE,{"disambiguationData":[TD([[subQ4,-1.0]])],"derivedFrom":subQ1}),1.0]])]});}
            var Q75;
            {var subQ0=sQuery(id+"F0.wireOp",EDGE,"E10.25.2");Q75=makeQuery(id+"F0.imprint","IMPRINT",FACE,{"disambiguationData":[TD([[makeQuery(id+"F0.imprint","IMPRINT",EDGE,{"derivedFrom":subQ0}),-1.0]])]});}
            var Q76;
            {var subQ1=sQuery(id+"F0.wireOp",EDGE,"E10.25.3");var subQ3=sQuery(id+"F0.wireOp",EDGE,"E10.25.7");var subQ4=makeQuery(id+"F0.imprint","INTERSECT",VERTEX,{"derivedFrom":[subQ1,subQ3]});Q76=makeQuery(id+"F0.imprint","IMPRINT",FACE,{"disambiguationData":[TD([[makeQuery(id+"F0.imprint","IMPRINT",EDGE,{"disambiguationData":[TD([[subQ4,-1.0]])],"derivedFrom":subQ1}),-1.0]])]});}
            var Q77;
            {var subQ1=sQuery(id+"F0.wireOp",EDGE,"E10.25.4");var subQ3=sQuery(id+"F0.wireOp",EDGE,"E10.25.7");var subQ4=makeQuery(id+"F0.imprint","INTERSECT",VERTEX,{"derivedFrom":[subQ1,subQ3]});Q77=makeQuery(id+"F0.imprint","IMPRINT",FACE,{"disambiguationData":[TD([[makeQuery(id+"F0.imprint","IMPRINT",EDGE,{"disambiguationData":[TD([[subQ4,-1.0]])],"derivedFrom":subQ1}),1.0]])]});}
            var Q78;
            {var subQ0=sQuery(id+"F0.wireOp",EDGE,"E10.26.2");Q78=makeQuery(id+"F0.imprint","IMPRINT",FACE,{"disambiguationData":[TD([[makeQuery(id+"F0.imprint","IMPRINT",EDGE,{"derivedFrom":subQ0}),-1.0]])]});}
            var Q79;
            {var subQ1=sQuery(id+"F0.wireOp",EDGE,"E10.26.3");var subQ3=sQuery(id+"F0.wireOp",EDGE,"E10.26.7");var subQ4=makeQuery(id+"F0.imprint","INTERSECT",VERTEX,{"derivedFrom":[subQ1,subQ3]});Q79=makeQuery(id+"F0.imprint","IMPRINT",FACE,{"disambiguationData":[TD([[makeQuery(id+"F0.imprint","IMPRINT",EDGE,{"disambiguationData":[TD([[subQ4,-1.0]])],"derivedFrom":subQ1}),-1.0]])]});}
            var Q80;
            {var subQ1=sQuery(id+"F0.wireOp",EDGE,"E10.26.4");var subQ3=sQuery(id+"F0.wireOp",EDGE,"E10.26.7");var subQ4=makeQuery(id+"F0.imprint","INTERSECT",VERTEX,{"derivedFrom":[subQ1,subQ3]});Q80=makeQuery(id+"F0.imprint","IMPRINT",FACE,{"disambiguationData":[TD([[makeQuery(id+"F0.imprint","IMPRINT",EDGE,{"disambiguationData":[TD([[subQ4,-1.0]])],"derivedFrom":subQ1}),1.0]])]});}
            var Q81;
            {var subQ0=sQuery(id+"F0.wireOp",EDGE,"E10.27.2");Q81=makeQuery(id+"F0.imprint","IMPRINT",FACE,{"disambiguationData":[TD([[makeQuery(id+"F0.imprint","IMPRINT",EDGE,{"derivedFrom":subQ0}),-1.0]])]});}
            var Q82;
            {var subQ1=sQuery(id+"F0.wireOp",EDGE,"E10.27.3");var subQ3=sQuery(id+"F0.wireOp",EDGE,"E10.27.7");var subQ4=makeQuery(id+"F0.imprint","INTERSECT",VERTEX,{"derivedFrom":[subQ1,subQ3]});Q82=makeQuery(id+"F0.imprint","IMPRINT",FACE,{"disambiguationData":[TD([[makeQuery(id+"F0.imprint","IMPRINT",EDGE,{"disambiguationData":[TD([[subQ4,-1.0]])],"derivedFrom":subQ1}),-1.0]])]});}
            var Q83;
            {var subQ1=sQuery(id+"F0.wireOp",EDGE,"E10.27.4");var subQ3=sQuery(id+"F0.wireOp",EDGE,"E10.27.7");var subQ4=makeQuery(id+"F0.imprint","INTERSECT",VERTEX,{"derivedFrom":[subQ1,subQ3]});Q83=makeQuery(id+"F0.imprint","IMPRINT",FACE,{"disambiguationData":[TD([[makeQuery(id+"F0.imprint","IMPRINT",EDGE,{"disambiguationData":[TD([[subQ4,-1.0]])],"derivedFrom":subQ1}),1.0]])]});}
            var Q84;
            Q84=makeQuery(id+"F0.imprint","IMPRINT",FACE,{"disambiguationData":[TD([[makeQuery(id+"F0.imprint","IMPRINT",EDGE,{"derivedFrom":sQuery(id+"F0.wireOp",EDGE,"E1")}),-1.0]])]});
            var Q85;
            {var subQ5=sQuery(id+"F0.wireOp",EDGE,"E10.1.8");Q85=makeQuery(id+"F0.imprint","IMPRINT",FACE,{"disambiguationData":[TD([[makeQuery(id+"F0.imprint","IMPRINT",EDGE,{"derivedFrom":subQ5}),1.0]])]});}
            var Q86;
            {var subQ0=sQuery(id+"F0.wireOp",EDGE,"E10.1.11");Q86=makeQuery(id+"F0.imprint","IMPRINT",FACE,{"disambiguationData":[TD([[makeQuery(id+"F0.imprint","IMPRINT",EDGE,{"derivedFrom":subQ0}),1.0]])]});}
            var Q87;
            {var subQ5=sQuery(id+"F0.wireOp",EDGE,"E10.2.8");Q87=makeQuery(id+"F0.imprint","IMPRINT",FACE,{"disambiguationData":[TD([[makeQuery(id+"F0.imprint","IMPRINT",EDGE,{"derivedFrom":subQ5}),1.0]])]});}
            var Q88;
            {var subQ0=sQuery(id+"F0.wireOp",EDGE,"E10.2.11");Q88=makeQuery(id+"F0.imprint","IMPRINT",FACE,{"disambiguationData":[TD([[makeQuery(id+"F0.imprint","IMPRINT",EDGE,{"derivedFrom":subQ0}),1.0]])]});}
            var Q89;
            {var subQ5=sQuery(id+"F0.wireOp",EDGE,"E10.3.8");Q89=makeQuery(id+"F0.imprint","IMPRINT",FACE,{"disambiguationData":[TD([[makeQuery(id+"F0.imprint","IMPRINT",EDGE,{"derivedFrom":subQ5}),1.0]])]});}
            var Q90;
            {var subQ0=sQuery(id+"F0.wireOp",EDGE,"E10.3.11");Q90=makeQuery(id+"F0.imprint","IMPRINT",FACE,{"disambiguationData":[TD([[makeQuery(id+"F0.imprint","IMPRINT",EDGE,{"derivedFrom":subQ0}),1.0]])]});}
            var Q91;
            {var subQ5=sQuery(id+"F0.wireOp",EDGE,"E10.4.8");Q91=makeQuery(id+"F0.imprint","IMPRINT",FACE,{"disambiguationData":[TD([[makeQuery(id+"F0.imprint","IMPRINT",EDGE,{"derivedFrom":subQ5}),1.0]])]});}
            var Q92;
            {var subQ0=sQuery(id+"F0.wireOp",EDGE,"E10.4.11");Q92=makeQuery(id+"F0.imprint","IMPRINT",FACE,{"disambiguationData":[TD([[makeQuery(id+"F0.imprint","IMPRINT",EDGE,{"derivedFrom":subQ0}),1.0]])]});}
            var Q93;
            {var subQ5=sQuery(id+"F0.wireOp",EDGE,"E10.5.8");Q93=makeQuery(id+"F0.imprint","IMPRINT",FACE,{"disambiguationData":[TD([[makeQuery(id+"F0.imprint","IMPRINT",EDGE,{"derivedFrom":subQ5}),1.0]])]});}
            var Q94;
            {var subQ0=sQuery(id+"F0.wireOp",EDGE,"E10.5.11");Q94=makeQuery(id+"F0.imprint","IMPRINT",FACE,{"disambiguationData":[TD([[makeQuery(id+"F0.imprint","IMPRINT",EDGE,{"derivedFrom":subQ0}),1.0]])]});}
            var Q95;
            {var subQ5=sQuery(id+"F0.wireOp",EDGE,"E10.6.8");Q95=makeQuery(id+"F0.imprint","IMPRINT",FACE,{"disambiguationData":[TD([[makeQuery(id+"F0.imprint","IMPRINT",EDGE,{"derivedFrom":subQ5}),1.0]])]});}
            var Q96;
            {var subQ0=sQuery(id+"F0.wireOp",EDGE,"E10.6.11");Q96=makeQuery(id+"F0.imprint","IMPRINT",FACE,{"disambiguationData":[TD([[makeQuery(id+"F0.imprint","IMPRINT",EDGE,{"derivedFrom":subQ0}),1.0]])]});}
            var Q97;
            {var subQ5=sQuery(id+"F0.wireOp",EDGE,"E10.7.8");Q97=makeQuery(id+"F0.imprint","IMPRINT",FACE,{"disambiguationData":[TD([[makeQuery(id+"F0.imprint","IMPRINT",EDGE,{"derivedFrom":subQ5}),1.0]])]});}
            var Q98;
            {var subQ0=sQuery(id+"F0.wireOp",EDGE,"E10.7.11");Q98=makeQuery(id+"F0.imprint","IMPRINT",FACE,{"disambiguationData":[TD([[makeQuery(id+"F0.imprint","IMPRINT",EDGE,{"derivedFrom":subQ0}),1.0]])]});}
            var Q99;
            {var subQ5=sQuery(id+"F0.wireOp",EDGE,"E10.8.8");Q99=makeQuery(id+"F0.imprint","IMPRINT",FACE,{"disambiguationData":[TD([[makeQuery(id+"F0.imprint","IMPRINT",EDGE,{"derivedFrom":subQ5}),1.0]])]});}
            var Q100;
            {var subQ0=sQuery(id+"F0.wireOp",EDGE,"E10.8.11");Q100=makeQuery(id+"F0.imprint","IMPRINT",FACE,{"disambiguationData":[TD([[makeQuery(id+"F0.imprint","IMPRINT",EDGE,{"derivedFrom":subQ0}),1.0]])]});}
            var Q101;
            {var subQ5=sQuery(id+"F0.wireOp",EDGE,"E10.9.8");Q101=makeQuery(id+"F0.imprint","IMPRINT",FACE,{"disambiguationData":[TD([[makeQuery(id+"F0.imprint","IMPRINT",EDGE,{"derivedFrom":subQ5}),1.0]])]});}
            var Q102;
            {var subQ0=sQuery(id+"F0.wireOp",EDGE,"E10.9.11");Q102=makeQuery(id+"F0.imprint","IMPRINT",FACE,{"disambiguationData":[TD([[makeQuery(id+"F0.imprint","IMPRINT",EDGE,{"derivedFrom":subQ0}),1.0]])]});}
            var Q103;
            {var subQ5=sQuery(id+"F0.wireOp",EDGE,"E10.10.8");Q103=makeQuery(id+"F0.imprint","IMPRINT",FACE,{"disambiguationData":[TD([[makeQuery(id+"F0.imprint","IMPRINT",EDGE,{"derivedFrom":subQ5}),1.0]])]});}
            var Q104;
            {var subQ0=sQuery(id+"F0.wireOp",EDGE,"E10.10.11");Q104=makeQuery(id+"F0.imprint","IMPRINT",FACE,{"disambiguationData":[TD([[makeQuery(id+"F0.imprint","IMPRINT",EDGE,{"derivedFrom":subQ0}),1.0]])]});}
            var Q105;
            {var subQ5=sQuery(id+"F0.wireOp",EDGE,"E10.11.8");Q105=makeQuery(id+"F0.imprint","IMPRINT",FACE,{"disambiguationData":[TD([[makeQuery(id+"F0.imprint","IMPRINT",EDGE,{"derivedFrom":subQ5}),1.0]])]});}
            var Q106;
            {var subQ0=sQuery(id+"F0.wireOp",EDGE,"E10.11.11");Q106=makeQuery(id+"F0.imprint","IMPRINT",FACE,{"disambiguationData":[TD([[makeQuery(id+"F0.imprint","IMPRINT",EDGE,{"derivedFrom":subQ0}),1.0]])]});}
            var Q107;
            {var subQ5=sQuery(id+"F0.wireOp",EDGE,"E10.12.8");Q107=makeQuery(id+"F0.imprint","IMPRINT",FACE,{"disambiguationData":[TD([[makeQuery(id+"F0.imprint","IMPRINT",EDGE,{"derivedFrom":subQ5}),1.0]])]});}
            var Q108;
            {var subQ0=sQuery(id+"F0.wireOp",EDGE,"E10.12.11");Q108=makeQuery(id+"F0.imprint","IMPRINT",FACE,{"disambiguationData":[TD([[makeQuery(id+"F0.imprint","IMPRINT",EDGE,{"derivedFrom":subQ0}),1.0]])]});}
            var Q109;
            {var subQ5=sQuery(id+"F0.wireOp",EDGE,"E10.13.8");Q109=makeQuery(id+"F0.imprint","IMPRINT",FACE,{"disambiguationData":[TD([[makeQuery(id+"F0.imprint","IMPRINT",EDGE,{"derivedFrom":subQ5}),1.0]])]});}
            var Q110;
            {var subQ0=sQuery(id+"F0.wireOp",EDGE,"E10.13.11");Q110=makeQuery(id+"F0.imprint","IMPRINT",FACE,{"disambiguationData":[TD([[makeQuery(id+"F0.imprint","IMPRINT",EDGE,{"derivedFrom":subQ0}),1.0]])]});}
            var Q111;
            {var subQ5=sQuery(id+"F0.wireOp",EDGE,"E10.14.8");Q111=makeQuery(id+"F0.imprint","IMPRINT",FACE,{"disambiguationData":[TD([[makeQuery(id+"F0.imprint","IMPRINT",EDGE,{"derivedFrom":subQ5}),1.0]])]});}
            var Q112;
            {var subQ5=sQuery(id+"F0.wireOp",EDGE,"E10.15.8");Q112=makeQuery(id+"F0.imprint","IMPRINT",FACE,{"disambiguationData":[TD([[makeQuery(id+"F0.imprint","IMPRINT",EDGE,{"derivedFrom":subQ5}),1.0]])]});}
            var Q113;
            {var subQ0=sQuery(id+"F0.wireOp",EDGE,"E10.15.11");Q113=makeQuery(id+"F0.imprint","IMPRINT",FACE,{"disambiguationData":[TD([[makeQuery(id+"F0.imprint","IMPRINT",EDGE,{"derivedFrom":subQ0}),1.0]])]});}
            var Q114;
            {var subQ5=sQuery(id+"F0.wireOp",EDGE,"E10.16.8");Q114=makeQuery(id+"F0.imprint","IMPRINT",FACE,{"disambiguationData":[TD([[makeQuery(id+"F0.imprint","IMPRINT",EDGE,{"derivedFrom":subQ5}),1.0]])]});}
            var Q115;
            {var subQ0=sQuery(id+"F0.wireOp",EDGE,"E10.16.11");Q115=makeQuery(id+"F0.imprint","IMPRINT",FACE,{"disambiguationData":[TD([[makeQuery(id+"F0.imprint","IMPRINT",EDGE,{"derivedFrom":subQ0}),1.0]])]});}
            var Q116;
            {var subQ5=sQuery(id+"F0.wireOp",EDGE,"E10.17.8");Q116=makeQuery(id+"F0.imprint","IMPRINT",FACE,{"disambiguationData":[TD([[makeQuery(id+"F0.imprint","IMPRINT",EDGE,{"derivedFrom":subQ5}),1.0]])]});}
            var Q117;
            {var subQ0=sQuery(id+"F0.wireOp",EDGE,"E10.17.11");Q117=makeQuery(id+"F0.imprint","IMPRINT",FACE,{"disambiguationData":[TD([[makeQuery(id+"F0.imprint","IMPRINT",EDGE,{"derivedFrom":subQ0}),1.0]])]});}
            var Q118;
            {var subQ5=sQuery(id+"F0.wireOp",EDGE,"E10.18.8");Q118=makeQuery(id+"F0.imprint","IMPRINT",FACE,{"disambiguationData":[TD([[makeQuery(id+"F0.imprint","IMPRINT",EDGE,{"derivedFrom":subQ5}),1.0]])]});}
            var Q119;
            {var subQ0=sQuery(id+"F0.wireOp",EDGE,"E10.18.11");Q119=makeQuery(id+"F0.imprint","IMPRINT",FACE,{"disambiguationData":[TD([[makeQuery(id+"F0.imprint","IMPRINT",EDGE,{"derivedFrom":subQ0}),1.0]])]});}
            var Q120;
            {var subQ5=sQuery(id+"F0.wireOp",EDGE,"E10.19.8");Q120=makeQuery(id+"F0.imprint","IMPRINT",FACE,{"disambiguationData":[TD([[makeQuery(id+"F0.imprint","IMPRINT",EDGE,{"derivedFrom":subQ5}),1.0]])]});}
            var Q121;
            {var subQ0=sQuery(id+"F0.wireOp",EDGE,"E10.19.11");Q121=makeQuery(id+"F0.imprint","IMPRINT",FACE,{"disambiguationData":[TD([[makeQuery(id+"F0.imprint","IMPRINT",EDGE,{"derivedFrom":subQ0}),1.0]])]});}
            var Q122;
            {var subQ5=sQuery(id+"F0.wireOp",EDGE,"E10.20.8");Q122=makeQuery(id+"F0.imprint","IMPRINT",FACE,{"disambiguationData":[TD([[makeQuery(id+"F0.imprint","IMPRINT",EDGE,{"derivedFrom":subQ5}),1.0]])]});}
            var Q123;
            {var subQ0=sQuery(id+"F0.wireOp",EDGE,"E10.20.11");Q123=makeQuery(id+"F0.imprint","IMPRINT",FACE,{"disambiguationData":[TD([[makeQuery(id+"F0.imprint","IMPRINT",EDGE,{"derivedFrom":subQ0}),1.0]])]});}
            var Q124;
            {var subQ5=sQuery(id+"F0.wireOp",EDGE,"E10.21.8");Q124=makeQuery(id+"F0.imprint","IMPRINT",FACE,{"disambiguationData":[TD([[makeQuery(id+"F0.imprint","IMPRINT",EDGE,{"derivedFrom":subQ5}),1.0]])]});}
            var Q125;
            {var subQ0=sQuery(id+"F0.wireOp",EDGE,"E10.21.11");Q125=makeQuery(id+"F0.imprint","IMPRINT",FACE,{"disambiguationData":[TD([[makeQuery(id+"F0.imprint","IMPRINT",EDGE,{"derivedFrom":subQ0}),1.0]])]});}
            var Q126;
            {var subQ5=sQuery(id+"F0.wireOp",EDGE,"E10.22.8");Q126=makeQuery(id+"F0.imprint","IMPRINT",FACE,{"disambiguationData":[TD([[makeQuery(id+"F0.imprint","IMPRINT",EDGE,{"derivedFrom":subQ5}),1.0]])]});}
            var Q127;
            {var subQ0=sQuery(id+"F0.wireOp",EDGE,"E10.22.11");Q127=makeQuery(id+"F0.imprint","IMPRINT",FACE,{"disambiguationData":[TD([[makeQuery(id+"F0.imprint","IMPRINT",EDGE,{"derivedFrom":subQ0}),1.0]])]});}
            var Q128;
            {var subQ5=sQuery(id+"F0.wireOp",EDGE,"E10.23.8");Q128=makeQuery(id+"F0.imprint","IMPRINT",FACE,{"disambiguationData":[TD([[makeQuery(id+"F0.imprint","IMPRINT",EDGE,{"derivedFrom":subQ5}),1.0]])]});}
            var Q129;
            {var subQ0=sQuery(id+"F0.wireOp",EDGE,"E10.23.11");Q129=makeQuery(id+"F0.imprint","IMPRINT",FACE,{"disambiguationData":[TD([[makeQuery(id+"F0.imprint","IMPRINT",EDGE,{"derivedFrom":subQ0}),1.0]])]});}
            var Q130;
            {var subQ5=sQuery(id+"F0.wireOp",EDGE,"E10.24.8");Q130=makeQuery(id+"F0.imprint","IMPRINT",FACE,{"disambiguationData":[TD([[makeQuery(id+"F0.imprint","IMPRINT",EDGE,{"derivedFrom":subQ5}),1.0]])]});}
            var Q131;
            {var subQ0=sQuery(id+"F0.wireOp",EDGE,"E10.24.11");Q131=makeQuery(id+"F0.imprint","IMPRINT",FACE,{"disambiguationData":[TD([[makeQuery(id+"F0.imprint","IMPRINT",EDGE,{"derivedFrom":subQ0}),1.0]])]});}
            var Q132;
            {var subQ5=sQuery(id+"F0.wireOp",EDGE,"E10.25.8");Q132=makeQuery(id+"F0.imprint","IMPRINT",FACE,{"disambiguationData":[TD([[makeQuery(id+"F0.imprint","IMPRINT",EDGE,{"derivedFrom":subQ5}),1.0]])]});}
            var Q133;
            {var subQ0=sQuery(id+"F0.wireOp",EDGE,"E10.25.11");Q133=makeQuery(id+"F0.imprint","IMPRINT",FACE,{"disambiguationData":[TD([[makeQuery(id+"F0.imprint","IMPRINT",EDGE,{"derivedFrom":subQ0}),1.0]])]});}
            var Q134;
            {var subQ5=sQuery(id+"F0.wireOp",EDGE,"E10.26.8");Q134=makeQuery(id+"F0.imprint","IMPRINT",FACE,{"disambiguationData":[TD([[makeQuery(id+"F0.imprint","IMPRINT",EDGE,{"derivedFrom":subQ5}),1.0]])]});}
            var Q135;
            {var subQ0=sQuery(id+"F0.wireOp",EDGE,"E10.26.11");Q135=makeQuery(id+"F0.imprint","IMPRINT",FACE,{"disambiguationData":[TD([[makeQuery(id+"F0.imprint","IMPRINT",EDGE,{"derivedFrom":subQ0}),1.0]])]});}
            var Q136;
            {var subQ5=sQuery(id+"F0.wireOp",EDGE,"E10.27.8");Q136=makeQuery(id+"F0.imprint","IMPRINT",FACE,{"disambiguationData":[TD([[makeQuery(id+"F0.imprint","IMPRINT",EDGE,{"derivedFrom":subQ5}),1.0]])]});}
            var Q137;
            {var subQ0=sQuery(id+"F0.wireOp",EDGE,"E10.27.11");Q137=makeQuery(id+"F0.imprint","IMPRINT",FACE,{"disambiguationData":[TD([[makeQuery(id+"F0.imprint","IMPRINT",EDGE,{"derivedFrom":subQ0}),1.0]])]});}
            var Q138;
            {var subQ0=sQuery(id+"F0.wireOp",EDGE,"E0");Q138=makeQuery(id+"F0.imprint","IMPRINT",FACE,{"disambiguationData":[TD([[makeQuery(id+"F0.imprint","IMPRINT",EDGE,{"derivedFrom":subQ0}),1.0]])]});}
            var Q139;
            {var subQ5=sQuery(id+"F0.wireOp",EDGE,"E3");Q139=makeQuery(id+"F0.imprint","IMPRINT",FACE,{"disambiguationData":[TD([[makeQuery(id+"F0.imprint","IMPRINT",EDGE,{"derivedFrom":subQ5}),1.0]])]});}
            var Q140;
            {var subQ0=sQuery(id+"F0.wireOp",EDGE,"E10.1.2");Q140=makeQuery(id+"F0.imprint","IMPRINT",FACE,{"disambiguationData":[TD([[makeQuery(id+"F0.imprint","IMPRINT",EDGE,{"derivedFrom":subQ0}),1.0]])]});}
            var Q141;
            {var subQ0=sQuery(id+"F0.wireOp",EDGE,"E10.2.2");Q141=makeQuery(id+"F0.imprint","IMPRINT",FACE,{"disambiguationData":[TD([[makeQuery(id+"F0.imprint","IMPRINT",EDGE,{"derivedFrom":subQ0}),1.0]])]});}
            var Q142;
            {var subQ0=sQuery(id+"F0.wireOp",EDGE,"E10.3.2");Q142=makeQuery(id+"F0.imprint","IMPRINT",FACE,{"disambiguationData":[TD([[makeQuery(id+"F0.imprint","IMPRINT",EDGE,{"derivedFrom":subQ0}),1.0]])]});}
            var Q143;
            {var subQ0=sQuery(id+"F0.wireOp",EDGE,"E10.4.2");Q143=makeQuery(id+"F0.imprint","IMPRINT",FACE,{"disambiguationData":[TD([[makeQuery(id+"F0.imprint","IMPRINT",EDGE,{"derivedFrom":subQ0}),1.0]])]});}
            var Q144;
            {var subQ0=sQuery(id+"F0.wireOp",EDGE,"E10.5.2");Q144=makeQuery(id+"F0.imprint","IMPRINT",FACE,{"disambiguationData":[TD([[makeQuery(id+"F0.imprint","IMPRINT",EDGE,{"derivedFrom":subQ0}),1.0]])]});}
            var Q145;
            {var subQ0=sQuery(id+"F0.wireOp",EDGE,"E10.6.2");Q145=makeQuery(id+"F0.imprint","IMPRINT",FACE,{"disambiguationData":[TD([[makeQuery(id+"F0.imprint","IMPRINT",EDGE,{"derivedFrom":subQ0}),1.0]])]});}
            var Q146;
            {var subQ0=sQuery(id+"F0.wireOp",EDGE,"E10.7.2");Q146=makeQuery(id+"F0.imprint","IMPRINT",FACE,{"disambiguationData":[TD([[makeQuery(id+"F0.imprint","IMPRINT",EDGE,{"derivedFrom":subQ0}),1.0]])]});}
            var Q147;
            {var subQ0=sQuery(id+"F0.wireOp",EDGE,"E10.8.2");Q147=makeQuery(id+"F0.imprint","IMPRINT",FACE,{"disambiguationData":[TD([[makeQuery(id+"F0.imprint","IMPRINT",EDGE,{"derivedFrom":subQ0}),1.0]])]});}
            var Q148;
            {var subQ0=sQuery(id+"F0.wireOp",EDGE,"E10.9.2");Q148=makeQuery(id+"F0.imprint","IMPRINT",FACE,{"disambiguationData":[TD([[makeQuery(id+"F0.imprint","IMPRINT",EDGE,{"derivedFrom":subQ0}),1.0]])]});}
            var Q149;
            {var subQ0=sQuery(id+"F0.wireOp",EDGE,"E10.10.2");Q149=makeQuery(id+"F0.imprint","IMPRINT",FACE,{"disambiguationData":[TD([[makeQuery(id+"F0.imprint","IMPRINT",EDGE,{"derivedFrom":subQ0}),1.0]])]});}
            var Q150;
            {var subQ0=sQuery(id+"F0.wireOp",EDGE,"E10.11.2");Q150=makeQuery(id+"F0.imprint","IMPRINT",FACE,{"disambiguationData":[TD([[makeQuery(id+"F0.imprint","IMPRINT",EDGE,{"derivedFrom":subQ0}),1.0]])]});}
            var Q151;
            {var subQ0=sQuery(id+"F0.wireOp",EDGE,"E10.12.2");Q151=makeQuery(id+"F0.imprint","IMPRINT",FACE,{"disambiguationData":[TD([[makeQuery(id+"F0.imprint","IMPRINT",EDGE,{"derivedFrom":subQ0}),1.0]])]});}
            var Q152;
            {var subQ0=sQuery(id+"F0.wireOp",EDGE,"E10.13.2");Q152=makeQuery(id+"F0.imprint","IMPRINT",FACE,{"disambiguationData":[TD([[makeQuery(id+"F0.imprint","IMPRINT",EDGE,{"derivedFrom":subQ0}),1.0]])]});}
            var Q153;
            {var subQ0=sQuery(id+"F0.wireOp",EDGE,"E10.14.2");Q153=makeQuery(id+"F0.imprint","IMPRINT",FACE,{"disambiguationData":[TD([[makeQuery(id+"F0.imprint","IMPRINT",EDGE,{"derivedFrom":subQ0}),1.0]])]});}
            var Q154;
            {var subQ0=sQuery(id+"F0.wireOp",EDGE,"E10.14.11");Q154=makeQuery(id+"F0.imprint","IMPRINT",FACE,{"disambiguationData":[TD([[makeQuery(id+"F0.imprint","IMPRINT",EDGE,{"derivedFrom":subQ0}),1.0]])]});}
            var Q155;
            {var subQ0=sQuery(id+"F0.wireOp",EDGE,"E10.15.2");Q155=makeQuery(id+"F0.imprint","IMPRINT",FACE,{"disambiguationData":[TD([[makeQuery(id+"F0.imprint","IMPRINT",EDGE,{"derivedFrom":subQ0}),1.0]])]});}
            var Q156;
            {var subQ0=sQuery(id+"F0.wireOp",EDGE,"E10.16.2");Q156=makeQuery(id+"F0.imprint","IMPRINT",FACE,{"disambiguationData":[TD([[makeQuery(id+"F0.imprint","IMPRINT",EDGE,{"derivedFrom":subQ0}),1.0]])]});}
            var Q157;
            {var subQ0=sQuery(id+"F0.wireOp",EDGE,"E10.17.2");Q157=makeQuery(id+"F0.imprint","IMPRINT",FACE,{"disambiguationData":[TD([[makeQuery(id+"F0.imprint","IMPRINT",EDGE,{"derivedFrom":subQ0}),1.0]])]});}
            var Q158;
            {var subQ0=sQuery(id+"F0.wireOp",EDGE,"E10.18.2");Q158=makeQuery(id+"F0.imprint","IMPRINT",FACE,{"disambiguationData":[TD([[makeQuery(id+"F0.imprint","IMPRINT",EDGE,{"derivedFrom":subQ0}),1.0]])]});}
            var Q159;
            {var subQ0=sQuery(id+"F0.wireOp",EDGE,"E10.19.2");Q159=makeQuery(id+"F0.imprint","IMPRINT",FACE,{"disambiguationData":[TD([[makeQuery(id+"F0.imprint","IMPRINT",EDGE,{"derivedFrom":subQ0}),1.0]])]});}
            var Q160;
            {var subQ0=sQuery(id+"F0.wireOp",EDGE,"E10.20.2");Q160=makeQuery(id+"F0.imprint","IMPRINT",FACE,{"disambiguationData":[TD([[makeQuery(id+"F0.imprint","IMPRINT",EDGE,{"derivedFrom":subQ0}),1.0]])]});}
            var Q161;
            {var subQ0=sQuery(id+"F0.wireOp",EDGE,"E10.21.2");Q161=makeQuery(id+"F0.imprint","IMPRINT",FACE,{"disambiguationData":[TD([[makeQuery(id+"F0.imprint","IMPRINT",EDGE,{"derivedFrom":subQ0}),1.0]])]});}
            var Q162;
            {var subQ0=sQuery(id+"F0.wireOp",EDGE,"E10.22.2");Q162=makeQuery(id+"F0.imprint","IMPRINT",FACE,{"disambiguationData":[TD([[makeQuery(id+"F0.imprint","IMPRINT",EDGE,{"derivedFrom":subQ0}),1.0]])]});}
            var Q163;
            {var subQ0=sQuery(id+"F0.wireOp",EDGE,"E10.23.2");Q163=makeQuery(id+"F0.imprint","IMPRINT",FACE,{"disambiguationData":[TD([[makeQuery(id+"F0.imprint","IMPRINT",EDGE,{"derivedFrom":subQ0}),1.0]])]});}
            var Q164;
            {var subQ0=sQuery(id+"F0.wireOp",EDGE,"E10.24.2");Q164=makeQuery(id+"F0.imprint","IMPRINT",FACE,{"disambiguationData":[TD([[makeQuery(id+"F0.imprint","IMPRINT",EDGE,{"derivedFrom":subQ0}),1.0]])]});}
            var Q165;
            {var subQ0=sQuery(id+"F0.wireOp",EDGE,"E10.25.2");Q165=makeQuery(id+"F0.imprint","IMPRINT",FACE,{"disambiguationData":[TD([[makeQuery(id+"F0.imprint","IMPRINT",EDGE,{"derivedFrom":subQ0}),1.0]])]});}
            var Q166;
            {var subQ0=sQuery(id+"F0.wireOp",EDGE,"E10.26.2");Q166=makeQuery(id+"F0.imprint","IMPRINT",FACE,{"disambiguationData":[TD([[makeQuery(id+"F0.imprint","IMPRINT",EDGE,{"derivedFrom":subQ0}),1.0]])]});}
            var Q167;
            {var subQ0=sQuery(id+"F0.wireOp",EDGE,"E10.27.2");Q167=makeQuery(id+"F0.imprint","IMPRINT",FACE,{"disambiguationData":[TD([[makeQuery(id+"F0.imprint","IMPRINT",EDGE,{"derivedFrom":subQ0}),1.0]])]});}
            var Q168;
            {var subQ76=sQuery(id+"F0.wireOp",EDGE,"E7.7.6");Q168=makeQuery(id+"F0.imprint","IMPRINT",FACE,{"disambiguationData":[TD([[makeQuery(id+"F0.imprint","IMPRINT",EDGE,{"derivedFrom":subQ76}),-1.0]])]});}
            var Q169;
            {var subQ85=sQuery(id+"F0.wireOp",EDGE,"E7.7.2");Q169=makeQuery(id+"F0.imprint","IMPRINT",FACE,{"disambiguationData":[TD([[makeQuery(id+"F0.imprint","IMPRINT",EDGE,{"derivedFrom":subQ85}),1.0]])]});}
            var Q170;
            {var subQ0=sQuery(id+"F0.wireOp",EDGE,"E10.16.14");Q170=makeQuery(id+"F0.imprint","IMPRINT",FACE,{"disambiguationData":[TD([[makeQuery(id+"F0.imprint","IMPRINT",EDGE,{"derivedFrom":subQ0}),1.0]])]});}
            var Q171;
            {var subQ0=sQuery(id+"F0.wireOp",EDGE,"E10.12.14");Q171=makeQuery(id+"F0.imprint","IMPRINT",FACE,{"disambiguationData":[TD([[makeQuery(id+"F0.imprint","IMPRINT",EDGE,{"derivedFrom":subQ0}),1.0]])]});}
            var Q172;
            {var subQ0=sQuery(id+"F0.wireOp",EDGE,"E10.11.14");Q172=makeQuery(id+"F0.imprint","IMPRINT",FACE,{"disambiguationData":[TD([[makeQuery(id+"F0.imprint","IMPRINT",EDGE,{"derivedFrom":subQ0}),1.0]])]});}
            var Q173;
            {var subQ0=sQuery(id+"F0.wireOp",EDGE,"E10.10.14");Q173=makeQuery(id+"F0.imprint","IMPRINT",FACE,{"disambiguationData":[TD([[makeQuery(id+"F0.imprint","IMPRINT",EDGE,{"derivedFrom":subQ0}),1.0]])]});}
            var Q174;
            Q174=makeQuery(id+"F0.imprint","IMPRINT",FACE,{"disambiguationData":[TD([[makeQuery(id+"F0.imprint","IMPRINT",EDGE,{"derivedFrom":sQuery(id+"F0.wireOp",EDGE,"E10.10.0")}),-1.0]])]});
            var Q175;
            {var subQ0=sQuery(id+"F0.wireOp",EDGE,"E10.9.14");Q175=makeQuery(id+"F0.imprint","IMPRINT",FACE,{"disambiguationData":[TD([[makeQuery(id+"F0.imprint","IMPRINT",EDGE,{"derivedFrom":subQ0}),1.0]])]});}
            var Q176;
            {var subQ0=sQuery(id+"F0.wireOp",EDGE,"E10.8.14");Q176=makeQuery(id+"F0.imprint","IMPRINT",FACE,{"disambiguationData":[TD([[makeQuery(id+"F0.imprint","IMPRINT",EDGE,{"derivedFrom":subQ0}),1.0]])]});}
            var Q177;
            {var subQ0=sQuery(id+"F0.wireOp",EDGE,"E10.20.14");Q177=makeQuery(id+"F0.imprint","IMPRINT",FACE,{"disambiguationData":[TD([[makeQuery(id+"F0.imprint","IMPRINT",EDGE,{"derivedFrom":subQ0}),1.0]])]});}
            var Q178;
            {var subQ0=sQuery(id+"F0.wireOp",EDGE,"E10.22.14");Q178=makeQuery(id+"F0.imprint","IMPRINT",FACE,{"disambiguationData":[TD([[makeQuery(id+"F0.imprint","IMPRINT",EDGE,{"derivedFrom":subQ0}),1.0]])]});}
            var Q179;
            {var subQ0=sQuery(id+"F0.wireOp",EDGE,"E10.5.14");Q179=makeQuery(id+"F0.imprint","IMPRINT",FACE,{"disambiguationData":[TD([[makeQuery(id+"F0.imprint","IMPRINT",EDGE,{"derivedFrom":subQ0}),1.0]])]});}
            var Q180;
            {var subQ0=sQuery(id+"F0.wireOp",EDGE,"E10.23.14");Q180=makeQuery(id+"F0.imprint","IMPRINT",FACE,{"disambiguationData":[TD([[makeQuery(id+"F0.imprint","IMPRINT",EDGE,{"derivedFrom":subQ0}),1.0]])]});}
            var Q181;
            {var subQ0=sQuery(id+"F0.wireOp",EDGE,"E10.4.14");Q181=makeQuery(id+"F0.imprint","IMPRINT",FACE,{"disambiguationData":[TD([[makeQuery(id+"F0.imprint","IMPRINT",EDGE,{"derivedFrom":subQ0}),1.0]])]});}
            var Q182;
            {var subQ0=sQuery(id+"F0.wireOp",EDGE,"E10.26.14");Q182=makeQuery(id+"F0.imprint","IMPRINT",FACE,{"disambiguationData":[TD([[makeQuery(id+"F0.imprint","IMPRINT",EDGE,{"derivedFrom":subQ0}),1.0]])]});}
            var Q183;
            Q183=makeQuery(id+"F0.imprint","IMPRINT",FACE,{"disambiguationData":[TD([[makeQuery(id+"F0.imprint","IMPRINT",EDGE,{"derivedFrom":sQuery(id+"F0.wireOp",EDGE,"E10.9.0")}),-1.0]])]});
            var Q184;
            Q184=makeQuery(id+"F0.imprint","IMPRINT",FACE,{"disambiguationData":[TD([[makeQuery(id+"F0.imprint","IMPRINT",EDGE,{"derivedFrom":sQuery(id+"F0.wireOp",EDGE,"E10.25.0")}),-1.0]])]});
            var Q185;
            {var subQ0=sQuery(id+"F0.wireOp",EDGE,"E10.14.14");Q185=makeQuery(id+"F0.imprint","IMPRINT",FACE,{"disambiguationData":[TD([[makeQuery(id+"F0.imprint","IMPRINT",EDGE,{"derivedFrom":subQ0}),1.0]])]});}
            var Q186;
            {var subQ0=sQuery(id+"F0.wireOp",EDGE,"E10.13.14");Q186=makeQuery(id+"F0.imprint","IMPRINT",FACE,{"disambiguationData":[TD([[makeQuery(id+"F0.imprint","IMPRINT",EDGE,{"derivedFrom":subQ0}),1.0]])]});}
            var Q187;
            {var subQ0=sQuery(id+"F0.wireOp",EDGE,"E10.15.14");Q187=makeQuery(id+"F0.imprint","IMPRINT",FACE,{"disambiguationData":[TD([[makeQuery(id+"F0.imprint","IMPRINT",EDGE,{"derivedFrom":subQ0}),1.0]])]});}
            var Q188;
            Q188=makeQuery(id+"F0.imprint","IMPRINT",FACE,{"disambiguationData":[TD([[makeQuery(id+"F0.imprint","IMPRINT",EDGE,{"derivedFrom":sQuery(id+"F0.wireOp",EDGE,"E10.13.0")}),-1.0]])]});
            var Q189;
            Q189=makeQuery(id+"F0.imprint","IMPRINT",FACE,{"disambiguationData":[TD([[makeQuery(id+"F0.imprint","IMPRINT",EDGE,{"derivedFrom":sQuery(id+"F0.wireOp",EDGE,"E10.15.0")}),-1.0]])]});
            var Q190;
            Q190=makeQuery(id+"F0.imprint","IMPRINT",FACE,{"disambiguationData":[TD([[makeQuery(id+"F0.imprint","IMPRINT",EDGE,{"derivedFrom":sQuery(id+"F0.wireOp",EDGE,"E10.16.0")}),-1.0]])]});
            var Q191;
            {var subQ0=sQuery(id+"F0.wireOp",EDGE,"E10.17.14");Q191=makeQuery(id+"F0.imprint","IMPRINT",FACE,{"disambiguationData":[TD([[makeQuery(id+"F0.imprint","IMPRINT",EDGE,{"derivedFrom":subQ0}),1.0]])]});}
            var Q192;
            Q192=makeQuery(id+"F0.imprint","IMPRINT",FACE,{"disambiguationData":[TD([[makeQuery(id+"F0.imprint","IMPRINT",EDGE,{"derivedFrom":sQuery(id+"F0.wireOp",EDGE,"E10.11.0")}),-1.0]])]});
            var Q193;
            {var subQ0=sQuery(id+"F0.wireOp",EDGE,"E10.18.14");Q193=makeQuery(id+"F0.imprint","IMPRINT",FACE,{"disambiguationData":[TD([[makeQuery(id+"F0.imprint","IMPRINT",EDGE,{"derivedFrom":subQ0}),1.0]])]});}
            var Q194;
            {var subQ0=sQuery(id+"F0.wireOp",EDGE,"E10.19.14");Q194=makeQuery(id+"F0.imprint","IMPRINT",FACE,{"disambiguationData":[TD([[makeQuery(id+"F0.imprint","IMPRINT",EDGE,{"derivedFrom":subQ0}),1.0]])]});}
            var Q195;
            Q195=makeQuery(id+"F0.imprint","IMPRINT",FACE,{"disambiguationData":[TD([[makeQuery(id+"F0.imprint","IMPRINT",EDGE,{"derivedFrom":sQuery(id+"F0.wireOp",EDGE,"E10.8.0")}),-1.0]])]});
            var Q196;
            Q196=makeQuery(id+"F0.imprint","IMPRINT",FACE,{"disambiguationData":[TD([[makeQuery(id+"F0.imprint","IMPRINT",EDGE,{"derivedFrom":sQuery(id+"F0.wireOp",EDGE,"E10.21.0")}),-1.0]])]});
            var Q197;
            Q197=makeQuery(id+"F0.imprint","IMPRINT",FACE,{"disambiguationData":[TD([[makeQuery(id+"F0.imprint","IMPRINT",EDGE,{"derivedFrom":sQuery(id+"F0.wireOp",EDGE,"E10.7.0")}),-1.0]])]});
            var Q198;
            {var subQ0=sQuery(id+"F0.wireOp",EDGE,"E10.7.14");Q198=makeQuery(id+"F0.imprint","IMPRINT",FACE,{"disambiguationData":[TD([[makeQuery(id+"F0.imprint","IMPRINT",EDGE,{"derivedFrom":subQ0}),1.0]])]});}
            var Q199;
            {var subQ0=sQuery(id+"F0.wireOp",EDGE,"E10.21.14");Q199=makeQuery(id+"F0.imprint","IMPRINT",FACE,{"disambiguationData":[TD([[makeQuery(id+"F0.imprint","IMPRINT",EDGE,{"derivedFrom":subQ0}),1.0]])]});}
            var Q200;
            Q200=makeQuery(id+"F0.imprint","IMPRINT",FACE,{"disambiguationData":[TD([[makeQuery(id+"F0.imprint","IMPRINT",EDGE,{"derivedFrom":sQuery(id+"F0.wireOp",EDGE,"E10.6.0")}),-1.0]])]});
            var Q201;
            {var subQ0=sQuery(id+"F0.wireOp",EDGE,"E10.6.14");Q201=makeQuery(id+"F0.imprint","IMPRINT",FACE,{"disambiguationData":[TD([[makeQuery(id+"F0.imprint","IMPRINT",EDGE,{"derivedFrom":subQ0}),1.0]])]});}
            var Q202;
            Q202=makeQuery(id+"F0.imprint","IMPRINT",FACE,{"disambiguationData":[TD([[makeQuery(id+"F0.imprint","IMPRINT",EDGE,{"derivedFrom":sQuery(id+"F0.wireOp",EDGE,"E10.5.0")}),-1.0]])]});
            var Q203;
            Q203=makeQuery(id+"F0.imprint","IMPRINT",FACE,{"disambiguationData":[TD([[makeQuery(id+"F0.imprint","IMPRINT",EDGE,{"derivedFrom":sQuery(id+"F0.wireOp",EDGE,"E10.24.0")}),-1.0]])]});
            var Q204;
            Q204=makeQuery(id+"F0.imprint","IMPRINT",FACE,{"disambiguationData":[TD([[makeQuery(id+"F0.imprint","IMPRINT",EDGE,{"derivedFrom":sQuery(id+"F0.wireOp",EDGE,"E10.4.0")}),-1.0]])]});
            var Q205;
            {var subQ0=sQuery(id+"F0.wireOp",EDGE,"E10.24.14");Q205=makeQuery(id+"F0.imprint","IMPRINT",FACE,{"disambiguationData":[TD([[makeQuery(id+"F0.imprint","IMPRINT",EDGE,{"derivedFrom":subQ0}),1.0]])]});}
            var Q206;
            Q206=makeQuery(id+"F0.imprint","IMPRINT",FACE,{"disambiguationData":[TD([[makeQuery(id+"F0.imprint","IMPRINT",EDGE,{"derivedFrom":sQuery(id+"F0.wireOp",EDGE,"E10.3.0")}),-1.0]])]});
            var Q207;
            {var subQ0=sQuery(id+"F0.wireOp",EDGE,"E10.25.14");Q207=makeQuery(id+"F0.imprint","IMPRINT",FACE,{"disambiguationData":[TD([[makeQuery(id+"F0.imprint","IMPRINT",EDGE,{"derivedFrom":subQ0}),1.0]])]});}
            var Q208;
            {var subQ0=sQuery(id+"F0.wireOp",EDGE,"E10.3.14");Q208=makeQuery(id+"F0.imprint","IMPRINT",FACE,{"disambiguationData":[TD([[makeQuery(id+"F0.imprint","IMPRINT",EDGE,{"derivedFrom":subQ0}),1.0]])]});}
            var Q209;
            Q209=makeQuery(id+"F0.imprint","IMPRINT",FACE,{"disambiguationData":[TD([[makeQuery(id+"F0.imprint","IMPRINT",EDGE,{"derivedFrom":sQuery(id+"F0.wireOp",EDGE,"E10.26.0")}),-1.0]])]});
            var Q210;
            Q210=makeQuery(id+"F0.imprint","IMPRINT",FACE,{"disambiguationData":[TD([[makeQuery(id+"F0.imprint","IMPRINT",EDGE,{"derivedFrom":sQuery(id+"F0.wireOp",EDGE,"E10.2.0")}),-1.0]])]});
            var Q211;
            Q211=makeQuery(id+"F0.imprint","IMPRINT",FACE,{"disambiguationData":[TD([[makeQuery(id+"F0.imprint","IMPRINT",EDGE,{"derivedFrom":sQuery(id+"F0.wireOp",EDGE,"E10.1.0")}),-1.0]])]});
            var Q212;
            Q212=makeQuery(id+"F0.imprint","IMPRINT",FACE,{"disambiguationData":[TD([[makeQuery(id+"F0.imprint","IMPRINT",EDGE,{"derivedFrom":sQuery(id+"F0.wireOp",EDGE,"E10.27.0")}),-1.0]])]});
            var Q213;
            {var subQ0=sQuery(id+"F0.wireOp",EDGE,"E10.2.14");Q213=makeQuery(id+"F0.imprint","IMPRINT",FACE,{"disambiguationData":[TD([[makeQuery(id+"F0.imprint","IMPRINT",EDGE,{"derivedFrom":subQ0}),1.0]])]});}
            var Q214;
            {var subQ0=sQuery(id+"F0.wireOp",EDGE,"E10.27.14");Q214=makeQuery(id+"F0.imprint","IMPRINT",FACE,{"disambiguationData":[TD([[makeQuery(id+"F0.imprint","IMPRINT",EDGE,{"derivedFrom":subQ0}),1.0]])]});}
            var Q215;
            {var subQ0=sQuery(id+"F0.wireOp",EDGE,"E10.1.14");Q215=makeQuery(id+"F0.imprint","IMPRINT",FACE,{"disambiguationData":[TD([[makeQuery(id+"F0.imprint","IMPRINT",EDGE,{"derivedFrom":subQ0}),1.0]])]});}
            var Q216;
            {var subQ0=sQuery(id+"F0.wireOp",EDGE,"E7.7.7");Q216=makeQuery(id+"F0.imprint","IMPRINT",FACE,{"disambiguationData":[TD([[makeQuery(id+"F0.imprint","IMPRINT",EDGE,{"derivedFrom":subQ0}),-1.0]])]});}
            var Q217;
            Q217=makeQuery(id+"F0.imprint","IMPRINT",FACE,{"disambiguationData":[TD([[makeQuery(id+"F0.imprint","IMPRINT",EDGE,{"derivedFrom":sQuery(id+"F0.wireOp",EDGE,"E10.14.0")}),-1.0]])]});
            var Q218;
            Q218=makeQuery(id+"F0.imprint","IMPRINT",FACE,{"disambiguationData":[TD([[makeQuery(id+"F0.imprint","IMPRINT",EDGE,{"derivedFrom":sQuery(id+"F0.wireOp",EDGE,"E10.12.0")}),-1.0]])]});
            var Q219;
            Q219=makeQuery(id+"F0.imprint","IMPRINT",FACE,{"disambiguationData":[TD([[makeQuery(id+"F0.imprint","IMPRINT",EDGE,{"derivedFrom":sQuery(id+"F0.wireOp",EDGE,"E10.17.0")}),-1.0]])]});
            var Q220;
            Q220=makeQuery(id+"F0.imprint","IMPRINT",FACE,{"disambiguationData":[TD([[makeQuery(id+"F0.imprint","IMPRINT",EDGE,{"derivedFrom":sQuery(id+"F0.wireOp",EDGE,"E10.18.0")}),-1.0]])]});
            var Q221;
            Q221=makeQuery(id+"F0.imprint","IMPRINT",FACE,{"disambiguationData":[TD([[makeQuery(id+"F0.imprint","IMPRINT",EDGE,{"derivedFrom":sQuery(id+"F0.wireOp",EDGE,"E10.19.0")}),-1.0]])]});
            var Q222;
            Q222=makeQuery(id+"F0.imprint","IMPRINT",FACE,{"disambiguationData":[TD([[makeQuery(id+"F0.imprint","IMPRINT",EDGE,{"derivedFrom":sQuery(id+"F0.wireOp",EDGE,"E10.20.0")}),-1.0]])]});
            var Q223;
            Q223=makeQuery(id+"F0.imprint","IMPRINT",FACE,{"disambiguationData":[TD([[makeQuery(id+"F0.imprint","IMPRINT",EDGE,{"derivedFrom":sQuery(id+"F0.wireOp",EDGE,"E10.22.0")}),-1.0]])]});
            var Q224;
            Q224=makeQuery(id+"F0.imprint","IMPRINT",FACE,{"disambiguationData":[TD([[makeQuery(id+"F0.imprint","IMPRINT",EDGE,{"derivedFrom":sQuery(id+"F0.wireOp",EDGE,"E10.23.0")}),-1.0]])]});
            var Q225;
            {var subQ1=sQuery(id+"F0.wireOp",EDGE,"E0");Q225=makeQuery(id+"F0.imprint","IMPRINT",FACE,{"disambiguationData":[TD([[makeQuery(id+"F0.imprint","IMPRINT",EDGE,{"derivedFrom":subQ1}),-1.0]])]});}
            extrude(context, id + "F1", {"entities" : qUnion([Q0, Q1, Q2, Q3, Q4, Q5, Q6, Q7, Q8, Q9, Q10, Q11, Q12, Q13, Q14, Q15, Q16, Q17, Q18, Q19, Q20, Q21, Q22, Q23, Q24, Q25, Q26, Q27, Q28, Q29, Q30, Q31, Q32, Q33, Q34, Q35, Q36, Q37, Q38, Q39, Q40, Q41, Q42, Q43, Q44, Q45, Q46, Q47, Q48, Q49, Q50, Q51, Q52, Q53, Q54, Q55, Q56, Q57, Q58, Q59, Q60, Q61, Q62, Q63, Q64, Q65, Q66, Q67, Q68, Q69, Q70, Q71, Q72, Q73, Q74, Q75, Q76, Q77, Q78, Q79, Q80, Q81, Q82, Q83, Q84, Q85, Q86, Q87, Q88, Q89, Q90, Q91, Q92, Q93, Q94, Q95, Q96, Q97, Q98, Q99, Q100, Q101, Q102, Q103, Q104, Q105, Q106, Q107, Q108, Q109, Q110, Q111, Q112, Q113, Q114, Q115, Q116, Q117, Q118, Q119, Q120, Q121, Q122, Q123, Q124, Q125, Q126, Q127, Q128, Q129, Q130, Q131, Q132, Q133, Q134, Q135, Q136, Q137, Q138, Q139, Q140, Q141, Q142, Q143, Q144, Q145, Q146, Q147, Q148, Q149, Q150, Q151, Q152, Q153, Q154, Q155, Q156, Q157, Q158, Q159, Q160, Q161, Q162, Q163, Q164, Q165, Q166, Q167, Q168, Q169, Q170, Q171, Q172, Q173, Q174, Q175, Q176, Q177, Q178, Q179, Q180, Q181, Q182, Q183, Q184, Q185, Q186, Q187, Q188, Q189, Q190, Q191, Q192, Q193, Q194, Q195, Q196, Q197, Q198, Q199, Q200, Q201, Q202, Q203, Q204, Q205, Q206, Q207, Q208, Q209, Q210, Q211, Q212, Q213, Q214, Q215, Q216, Q217, Q218, Q219, Q220, Q221, Q222, Q223, Q224, Q225]), "depth" : 7 * mm});
        }
        {
            var Q0;
            Q0=makeQuery(id+"F1.opExtrude","CAP_FACE",FACE,{"disambiguationData":[OSD([sQuery(id+"F0.wireOp",EDGE,"E1"),sQuery(id+"F0.wireOp",EDGE,"E2"),sQuery(id+"F0.wireOp",EDGE,"E4"),sQuery(id+"F0.wireOp",EDGE,"E5"),sQuery(id+"F0.wireOp",EDGE,"E6"),sQuery(id+"F0.wireOp",EDGE,"E7.7.1"),sQuery(id+"F0.wireOp",EDGE,"E2"),sQuery(id+"F0.wireOp",EDGE,"E10.1.5"),sQuery(id+"F0.wireOp",EDGE,"E10.1.6"),sQuery(id+"F0.wireOp",EDGE,"E10.1.8"),sQuery(id+"F0.wireOp",EDGE,"E10.1.9"),sQuery(id+"F0.wireOp",EDGE,"E10.1.13"),sQuery(id+"F0.wireOp",EDGE,"E10.2.5"),sQuery(id+"F0.wireOp",EDGE,"E10.2.6"),sQuery(id+"F0.wireOp",EDGE,"E10.2.8"),sQuery(id+"F0.wireOp",EDGE,"E10.2.9"),sQuery(id+"F0.wireOp",EDGE,"E10.2.13"),sQuery(id+"F0.wireOp",EDGE,"E10.3.5"),sQuery(id+"F0.wireOp",EDGE,"E10.3.6"),sQuery(id+"F0.wireOp",EDGE,"E10.3.8"),sQuery(id+"F0.wireOp",EDGE,"E10.3.9"),sQuery(id+"F0.wireOp",EDGE,"E10.3.13"),sQuery(id+"F0.wireOp",EDGE,"E10.4.5"),sQuery(id+"F0.wireOp",EDGE,"E10.4.6"),sQuery(id+"F0.wireOp",EDGE,"E10.4.8"),sQuery(id+"F0.wireOp",EDGE,"E10.4.9"),sQuery(id+"F0.wireOp",EDGE,"E10.4.13"),sQuery(id+"F0.wireOp",EDGE,"E10.5.5"),sQuery(id+"F0.wireOp",EDGE,"E10.5.6"),sQuery(id+"F0.wireOp",EDGE,"E10.5.8"),sQuery(id+"F0.wireOp",EDGE,"E10.5.9"),sQuery(id+"F0.wireOp",EDGE,"E10.5.13"),sQuery(id+"F0.wireOp",EDGE,"E10.6.5"),sQuery(id+"F0.wireOp",EDGE,"E10.6.6"),sQuery(id+"F0.wireOp",EDGE,"E10.6.8"),sQuery(id+"F0.wireOp",EDGE,"E10.6.9"),sQuery(id+"F0.wireOp",EDGE,"E10.6.13"),sQuery(id+"F0.wireOp",EDGE,"E10.7.5"),sQuery(id+"F0.wireOp",EDGE,"E10.7.6"),sQuery(id+"F0.wireOp",EDGE,"E10.7.8"),sQuery(id+"F0.wireOp",EDGE,"E10.7.9"),sQuery(id+"F0.wireOp",EDGE,"E10.7.13"),sQuery(id+"F0.wireOp",EDGE,"E10.8.5"),sQuery(id+"F0.wireOp",EDGE,"E10.8.6"),sQuery(id+"F0.wireOp",EDGE,"E10.8.8"),sQuery(id+"F0.wireOp",EDGE,"E10.8.9"),sQuery(id+"F0.wireOp",EDGE,"E10.8.13"),sQuery(id+"F0.wireOp",EDGE,"E10.9.5"),sQuery(id+"F0.wireOp",EDGE,"E10.9.6"),sQuery(id+"F0.wireOp",EDGE,"E10.9.8"),sQuery(id+"F0.wireOp",EDGE,"E10.9.9"),sQuery(id+"F0.wireOp",EDGE,"E10.9.13"),sQuery(id+"F0.wireOp",EDGE,"E10.10.5"),sQuery(id+"F0.wireOp",EDGE,"E10.10.6"),sQuery(id+"F0.wireOp",EDGE,"E10.10.8"),sQuery(id+"F0.wireOp",EDGE,"E10.10.9"),sQuery(id+"F0.wireOp",EDGE,"E10.10.13"),sQuery(id+"F0.wireOp",EDGE,"E10.11.5"),sQuery(id+"F0.wireOp",EDGE,"E10.11.6"),sQuery(id+"F0.wireOp",EDGE,"E10.11.8"),sQuery(id+"F0.wireOp",EDGE,"E10.11.9"),sQuery(id+"F0.wireOp",EDGE,"E10.11.13"),sQuery(id+"F0.wireOp",EDGE,"E10.12.5"),sQuery(id+"F0.wireOp",EDGE,"E10.12.6"),sQuery(id+"F0.wireOp",EDGE,"E10.12.8"),sQuery(id+"F0.wireOp",EDGE,"E10.12.9"),sQuery(id+"F0.wireOp",EDGE,"E10.12.13"),sQuery(id+"F0.wireOp",EDGE,"E10.13.5"),sQuery(id+"F0.wireOp",EDGE,"E10.13.6"),sQuery(id+"F0.wireOp",EDGE,"E10.13.8"),sQuery(id+"F0.wireOp",EDGE,"E10.13.9"),sQuery(id+"F0.wireOp",EDGE,"E10.13.13"),sQuery(id+"F0.wireOp",EDGE,"E10.14.5"),sQuery(id+"F0.wireOp",EDGE,"E10.14.6"),sQuery(id+"F0.wireOp",EDGE,"E10.14.8"),sQuery(id+"F0.wireOp",EDGE,"E10.14.9"),sQuery(id+"F0.wireOp",EDGE,"E10.14.13"),sQuery(id+"F0.wireOp",EDGE,"E10.15.5"),sQuery(id+"F0.wireOp",EDGE,"E10.15.6"),sQuery(id+"F0.wireOp",EDGE,"E10.15.8"),sQuery(id+"F0.wireOp",EDGE,"E10.15.9"),sQuery(id+"F0.wireOp",EDGE,"E10.15.13"),sQuery(id+"F0.wireOp",EDGE,"E10.16.5"),sQuery(id+"F0.wireOp",EDGE,"E10.16.6"),sQuery(id+"F0.wireOp",EDGE,"E10.16.8"),sQuery(id+"F0.wireOp",EDGE,"E10.16.9"),sQuery(id+"F0.wireOp",EDGE,"E10.16.13"),sQuery(id+"F0.wireOp",EDGE,"E10.17.5"),sQuery(id+"F0.wireOp",EDGE,"E10.17.6"),sQuery(id+"F0.wireOp",EDGE,"E10.17.8"),sQuery(id+"F0.wireOp",EDGE,"E10.17.9"),sQuery(id+"F0.wireOp",EDGE,"E10.17.13"),sQuery(id+"F0.wireOp",EDGE,"E10.18.5"),sQuery(id+"F0.wireOp",EDGE,"E10.18.6"),sQuery(id+"F0.wireOp",EDGE,"E10.18.8"),sQuery(id+"F0.wireOp",EDGE,"E10.18.9"),sQuery(id+"F0.wireOp",EDGE,"E10.18.13"),sQuery(id+"F0.wireOp",EDGE,"E10.19.5"),sQuery(id+"F0.wireOp",EDGE,"E10.19.6"),sQuery(id+"F0.wireOp",EDGE,"E10.19.8"),sQuery(id+"F0.wireOp",EDGE,"E10.19.9"),sQuery(id+"F0.wireOp",EDGE,"E10.19.13"),sQuery(id+"F0.wireOp",EDGE,"E10.20.5"),sQuery(id+"F0.wireOp",EDGE,"E10.20.6"),sQuery(id+"F0.wireOp",EDGE,"E10.20.8"),sQuery(id+"F0.wireOp",EDGE,"E10.20.9"),sQuery(id+"F0.wireOp",EDGE,"E10.20.13"),sQuery(id+"F0.wireOp",EDGE,"E10.21.5"),sQuery(id+"F0.wireOp",EDGE,"E10.21.6"),sQuery(id+"F0.wireOp",EDGE,"E10.21.8"),sQuery(id+"F0.wireOp",EDGE,"E10.21.9"),sQuery(id+"F0.wireOp",EDGE,"E10.21.13"),sQuery(id+"F0.wireOp",EDGE,"E10.22.5"),sQuery(id+"F0.wireOp",EDGE,"E10.22.6"),sQuery(id+"F0.wireOp",EDGE,"E10.22.8"),sQuery(id+"F0.wireOp",EDGE,"E10.22.9"),sQuery(id+"F0.wireOp",EDGE,"E10.22.13"),sQuery(id+"F0.wireOp",EDGE,"E10.23.5"),sQuery(id+"F0.wireOp",EDGE,"E10.23.6"),sQuery(id+"F0.wireOp",EDGE,"E10.23.8"),sQuery(id+"F0.wireOp",EDGE,"E10.23.9"),sQuery(id+"F0.wireOp",EDGE,"E10.23.13"),sQuery(id+"F0.wireOp",EDGE,"E10.24.5"),sQuery(id+"F0.wireOp",EDGE,"E10.24.6"),sQuery(id+"F0.wireOp",EDGE,"E10.24.8"),sQuery(id+"F0.wireOp",EDGE,"E10.24.9"),sQuery(id+"F0.wireOp",EDGE,"E10.24.13"),sQuery(id+"F0.wireOp",EDGE,"E10.25.5"),sQuery(id+"F0.wireOp",EDGE,"E10.25.6"),sQuery(id+"F0.wireOp",EDGE,"E10.25.8"),sQuery(id+"F0.wireOp",EDGE,"E10.25.9"),sQuery(id+"F0.wireOp",EDGE,"E10.25.13"),sQuery(id+"F0.wireOp",EDGE,"E10.26.5"),sQuery(id+"F0.wireOp",EDGE,"E10.26.6"),sQuery(id+"F0.wireOp",EDGE,"E10.26.8"),sQuery(id+"F0.wireOp",EDGE,"E10.26.9"),sQuery(id+"F0.wireOp",EDGE,"E10.26.13"),sQuery(id+"F0.wireOp",EDGE,"E10.27.5"),sQuery(id+"F0.wireOp",EDGE,"E10.27.6"),sQuery(id+"F0.wireOp",EDGE,"E10.27.8"),sQuery(id+"F0.wireOp",EDGE,"E10.27.9"),sQuery(id+"F0.wireOp",EDGE,"E10.27.13"),sQuery(id+"F0.wireOp",EDGE,"E11")])],"isStart":false});
            var sketch = newSketch(context, id + "F2", { "sketchPlane" : qUnion([Q0])});
            skCircle(sketch, "E12", {"center": v(-36.67, 17.6) * mm, "radius": 11.7 * mm});
            skSolve(sketch);
        }
        {
            var Q0;
            Q0=makeQuery(id+"F2.imprint","IMPRINT",FACE,{"disambiguationData":[TD([[makeQuery(id+"F2.imprint","IMPRINT",EDGE,{"derivedFrom":sQuery(id+"F2.wireOp",EDGE,"E12")}),1.0]])]});
            extrude(context, id + "F3", {"entities" : qUnion([Q0]), "operationType" : NewBodyOperationType.REMOVE, "oppositeDirection" : true, "depth" : 6 * mm});
        }
        {
            var Q0;
            {var subQ85=sQuery(id+"F0.wireOp",EDGE,"E7.7.2");Q0=makeQuery(id+"F0.imprint","IMPRINT",FACE,{"disambiguationData":[TD([[makeQuery(id+"F0.imprint","IMPRINT",EDGE,{"derivedFrom":subQ85}),1.0]])]});}
            var sketch = newSketch(context, id + "F4", { "sketchPlane" : qUnion([Q0])});
            skCircle(sketch, "E13", {"center": v(-36.67, 17.6) * mm, "radius": 2.95 * mm});
            skCircle(sketch, "E14", {"center": v(-36.67, 17.6) * mm, "radius": 4.45 * mm});
            skSolve(sketch);
        }
        {
            var Q0;
            Q0 = qSketchRegion(id + "F4", true);
            extrude(context, id + "F5", {"entities" : qUnion([Q0]), "operationType" : NewBodyOperationType.ADD, "depth" : 11.9 * mm});
        }
        {
            var Q0;
            {var subQ0=sQuery(id+"F4.wireOp",EDGE,"E13");var subQ1=makeQuery(id+"F0.imprint","IMPRINT",EDGE,{"derivedFrom":sQuery(id+"F0.wireOp",EDGE,"E8")});var subQ2=makeQuery(id+"F4.imprint","INTERSECT",VERTEX,{"derivedFrom":[subQ1,subQ0]});Q0=makeQuery(id+"F4.imprint","IMPRINT",FACE,{"disambiguationData":[TD([[makeQuery(id+"F4.imprint","IMPRINT",EDGE,{"disambiguationData":[TD([[subQ2,1.0]])],"derivedFrom":subQ0}),1.0]])]});}
            var Q1;
            {var subQ0=sQuery(id+"F4.wireOp",EDGE,"E13");var subQ1=makeQuery(id+"F0.imprint","IMPRINT",EDGE,{"derivedFrom":sQuery(id+"F0.wireOp",EDGE,"E8")});var subQ2=makeQuery(id+"F4.imprint","INTERSECT",VERTEX,{"derivedFrom":[subQ1,subQ0]});Q1=makeQuery(id+"F4.imprint","IMPRINT",FACE,{"disambiguationData":[TD([[makeQuery(id+"F4.imprint","IMPRINT",EDGE,{"disambiguationData":[TD([[subQ2,-1.0]])],"derivedFrom":subQ0}),1.0]])]});}
            extrude(context, id + "F6", {"entities" : qUnion([Q0, Q1]), "operationType" : NewBodyOperationType.REMOVE, "depth" : 25.4 * mm});
        }
    });
